annotation { "Feature Type Name" : "Feature", "Feature Type Description" : "" }
export const myFeature = defineFeature(function(context is Context, id is Id, definition is map)
    precondition{}
    {
        {
            var Q0;
            Q0=qCreatedBy(makeId("Top.planeOp"),FACE);
            var sketch = newSketch(context, id + "F0", { "sketchPlane" : qUnion([Q0])});
            skLineSegment(sketch, "E0.bottom", {"start": v(0, 0) * mm, "end": v(22.86, 0) * mm});
            skLineSegment(sketch, "E0.top", {"start": v(2.54, 25.4) * mm, "end": v(20.32, 25.4) * mm});
            skLineSegment(sketch, "E0.left", {"start": v(0, 0) * mm, "end": v(0, 22.86) * mm});
            skLineSegment(sketch, "E0.right", {"start": v(22.86, 0) * mm, "end": v(22.86, 22.86) * mm});
            skPoint(sketch, "E1.visualSharp", {"position": v(0, 25.4) * mm});
            skArc(sketch, "E1.filletArc", {"start": v(2.54, 25.4) * mm, "mid": v(0.74, 24.66) * mm, "end": v(0, 22.86) * mm});
            skPoint(sketch, "E2.visualSharp", {"position": v(22.86, 25.4) * mm});
            skArc(sketch, "E2.filletArc", {"start": v(22.86, 22.86) * mm, "mid": v(22.12, 24.66) * mm, "end": v(20.32, 25.4) * mm});
            skCircle(sketch, "E3", {"center": v(11.43, 2.54) * mm, "radius": 0.5 * mm});
            skPoint(sketch, "E4", {"position": v(11.43, 0) * mm});
            skCircle(sketch, "E5.1.0.0", {"center": v(13.97, 2.54) * mm, "radius": 0.5 * mm});
            skCircle(sketch, "E5.2.0.0", {"center": v(16.51, 2.54) * mm, "radius": 0.5 * mm});
            skCircle(sketch, "E5.3.0.0", {"center": v(19.05, 2.54) * mm, "radius": 0.5 * mm});
            skCircle(sketch, "E5.4.0.0", {"center": v(21.6, 2.54) * mm, "radius": 0.5 * mm});
            skLineSegment(sketch, "E5.direction1", {"start": v(11.43, 2.54) * mm, "end": v(13.97, 2.54) * mm, "construction": true});
            skCircle(sketch, "E6.1.0.0", {"center": v(8.9, 2.54) * mm, "radius": 0.5 * mm});
            skCircle(sketch, "E6.2.0.0", {"center": v(6.35, 2.54) * mm, "radius": 0.5 * mm});
            skCircle(sketch, "E6.3.0.0", {"center": v(3.8, 2.54) * mm, "radius": 0.5 * mm});
            skCircle(sketch, "E6.4.0.0", {"center": v(1.27, 2.54) * mm, "radius": 0.5 * mm});
            skLineSegment(sketch, "E6.direction1", {"start": v(11.43, 2.54) * mm, "end": v(8.9, 2.54) * mm, "construction": true});
            skCircle(sketch, "E7", {"center": v(2.54, 22.86) * mm, "radius": 1.27 * mm});
            skCircle(sketch, "E8", {"center": v(20.32, 22.86) * mm, "radius": 1.27 * mm});
            skLineSegment(sketch, "E9.bottom", {"start": v(-8.9, 0) * mm, "end": v(-24.13, 0) * mm});
            skLineSegment(sketch, "E9.top", {"start": v(-8.9, 20.32) * mm, "end": v(-24.13, 20.32) * mm});
            skLineSegment(sketch, "E9.left", {"start": v(-6.35, 2.54) * mm, "end": v(-6.35, 17.78) * mm});
            skLineSegment(sketch, "E9.right", {"start": v(-26.67, 2.54) * mm, "end": v(-26.67, 17.78) * mm});
            skPoint(sketch, "E10.visualSharp", {"position": v(-26.67, 20.32) * mm});
            skArc(sketch, "E10.filletArc", {"start": v(-24.13, 20.32) * mm, "mid": v(-25.93, 19.58) * mm, "end": v(-26.67, 17.78) * mm});
            skPoint(sketch, "E11.visualSharp", {"position": v(-6.35, 20.32) * mm});
            skArc(sketch, "E11.filletArc", {"start": v(-6.35, 17.78) * mm, "mid": v(-7.1, 19.58) * mm, "end": v(-8.9, 20.32) * mm});
            skPoint(sketch, "E12.visualSharp", {"position": v(-6.35, 0) * mm});
            skArc(sketch, "E12.filletArc", {"start": v(-8.9, 0) * mm, "mid": v(-7.1, 0.74) * mm, "end": v(-6.35, 2.54) * mm});
            skPoint(sketch, "E13.visualSharp", {"position": v(-26.67, 0) * mm});
            skArc(sketch, "E13.filletArc", {"start": v(-26.67, 2.54) * mm, "mid": v(-25.93, 0.74) * mm, "end": v(-24.13, 0) * mm});
            skCircle(sketch, "E14", {"center": v(-24.13, 17.78) * mm, "radius": 1.27 * mm});
            skCircle(sketch, "E15", {"center": v(-8.89, 17.78) * mm, "radius": 1.27 * mm});
            skCircle(sketch, "E16", {"center": v(-25.4, 2.54) * mm, "radius": 0.5 * mm});
            skCircle(sketch, "E17.1.0.0", {"center": v(-22.86, 2.54) * mm, "radius": 0.5 * mm});
            skCircle(sketch, "E17.2.0.0", {"center": v(-20.32, 2.54) * mm, "radius": 0.5 * mm});
            skCircle(sketch, "E17.3.0.0", {"center": v(-17.78, 2.54) * mm, "radius": 0.5 * mm});
            skCircle(sketch, "E17.4.0.0", {"center": v(-15.24, 2.54) * mm, "radius": 0.5 * mm});
            skCircle(sketch, "E17.5.0.0", {"center": v(-12.7, 2.54) * mm, "radius": 0.5 * mm});
            skCircle(sketch, "E17.6.0.0", {"center": v(-10.16, 2.54) * mm, "radius": 0.5 * mm});
            skCircle(sketch, "E17.7.0.0", {"center": v(-7.62, 2.54) * mm, "radius": 0.5 * mm});
            skLineSegment(sketch, "E17.direction1", {"start": v(-25.4, 2.54) * mm, "end": v(-22.86, 2.54) * mm, "construction": true});
            skLineSegment(sketch, "E18.bottom", {"start": v(-8.89, -6.35) * mm, "end": v(-24.13, -6.35) * mm});
            skLineSegment(sketch, "E18.top", {"start": v(-8.89, -26.67) * mm, "end": v(-24.13, -26.67) * mm});
            skLineSegment(sketch, "E18.left", {"start": v(-6.35, -8.89) * mm, "end": v(-6.35, -24.13) * mm});
            skLineSegment(sketch, "E18.right", {"start": v(-26.67, -8.9) * mm, "end": v(-26.67, -24.13) * mm});
            skPoint(sketch, "E19.visualSharp", {"position": v(-26.67, -6.35) * mm});
            skArc(sketch, "E19.filletArc", {"start": v(-24.13, -6.35) * mm, "mid": v(-25.93, -7.1) * mm, "end": v(-26.67, -8.9) * mm});
            skPoint(sketch, "E20.visualSharp", {"position": v(-6.35, -6.35) * mm});
            skArc(sketch, "E20.filletArc", {"start": v(-6.35, -8.89) * mm, "mid": v(-7.1, -7.1) * mm, "end": v(-8.89, -6.35) * mm});
            skPoint(sketch, "E21.visualSharp", {"position": v(-6.35, -26.67) * mm});
            skArc(sketch, "E21.filletArc", {"start": v(-8.89, -26.67) * mm, "mid": v(-7.1, -25.93) * mm, "end": v(-6.35, -24.13) * mm});
            skPoint(sketch, "E22.visualSharp", {"position": v(-26.67, -26.67) * mm});
            skArc(sketch, "E22.filletArc", {"start": v(-26.67, -24.13) * mm, "mid": v(-25.93, -25.93) * mm, "end": v(-24.13, -26.67) * mm});
            skCircle(sketch, "E23", {"center": v(-24.13, -8.9) * mm, "radius": 1.27 * mm});
            skCircle(sketch, "E24", {"center": v(-8.89, -8.89) * mm, "radius": 1.27 * mm});
            skCircle(sketch, "E25", {"center": v(-16.5, -25.15) * mm, "radius": 0.5 * mm});
            skPoint(sketch, "E25.centerSnap0", {"position": v(-16.5, -26.67) * mm});
            skCircle(sketch, "E26.1.0.0", {"center": v(-13.97, -25.15) * mm, "radius": 0.5 * mm});
            skCircle(sketch, "E26.2.0.0", {"center": v(-11.43, -25.15) * mm, "radius": 0.5 * mm});
            skCircle(sketch, "E26.3.0.0", {"center": v(-8.89, -25.15) * mm, "radius": 0.5 * mm});
            skLineSegment(sketch, "E26.direction1", {"start": v(-16.51, -25.15) * mm, "end": v(-13.97, -25.15) * mm, "construction": true});
            skCircle(sketch, "E27.1.0.0", {"center": v(-19.05, -25.15) * mm, "radius": 0.5 * mm});
            skCircle(sketch, "E27.2.0.0", {"center": v(-21.59, -25.15) * mm, "radius": 0.5 * mm});
            skCircle(sketch, "E27.3.0.0", {"center": v(-24.13, -25.15) * mm, "radius": 0.5 * mm});
            skLineSegment(sketch, "E27.direction1", {"start": v(-16.51, -25.15) * mm, "end": v(-19.05, -25.15) * mm, "construction": true});
            skCircle(sketch, "E28", {"center": v(-15.24, 15.24) * mm, "radius": 0.5 * mm});
            skCircle(sketch, "E29", {"center": v(-17.78, 15.24) * mm, "radius": 0.5 * mm});
            skCircle(sketch, "E30", {"center": v(-12.7, 15.24) * mm, "radius": 0.5 * mm});
            skLineSegment(sketch, "E31.bottom", {"start": v(2.54, -6.35) * mm, "end": v(21.59, -6.35) * mm});
            skLineSegment(sketch, "E31.top", {"start": v(2.54, -34.3) * mm, "end": v(21.59, -34.3) * mm});
            skLineSegment(sketch, "E31.left", {"start": v(0, -8.9) * mm, "end": v(0, -31.75) * mm});
            skLineSegment(sketch, "E31.right", {"start": v(24.13, -8.89) * mm, "end": v(24.13, -31.75) * mm});
            skPoint(sketch, "E32.visualSharp", {"position": v(0, -6.35) * mm});
            skArc(sketch, "E32.filletArc", {"start": v(2.54, -6.35) * mm, "mid": v(0.74, -7.1) * mm, "end": v(0, -8.9) * mm});
            skPoint(sketch, "E33.visualSharp", {"position": v(24.13, -6.35) * mm});
            skArc(sketch, "E33.filletArc", {"start": v(24.13, -8.89) * mm, "mid": v(23.39, -7.1) * mm, "end": v(21.59, -6.35) * mm});
            skPoint(sketch, "E34.visualSharp", {"position": v(0, -34.3) * mm});
            skArc(sketch, "E34.filletArc", {"start": v(0, -31.75) * mm, "mid": v(0.74, -33.55) * mm, "end": v(2.54, -34.3) * mm});
            skPoint(sketch, "E35.visualSharp", {"position": v(24.13, -34.3) * mm});
            skArc(sketch, "E35.filletArc", {"start": v(21.59, -34.3) * mm, "mid": v(23.39, -33.55) * mm, "end": v(24.13, -31.75) * mm});
            skCircle(sketch, "E36", {"center": v(21.59, -8.89) * mm, "radius": 1.27 * mm});
            skCircle(sketch, "E37", {"center": v(21.59, -31.75) * mm, "radius": 1.27 * mm});
            skCircle(sketch, "E38", {"center": v(2.54, -20.32) * mm, "radius": 0.5 * mm});
            skPoint(sketch, "E38.centerSnap0", {"position": v(0, -20.32) * mm});
            skCircle(sketch, "E39.0.1.0", {"center": v(2.54, -17.78) * mm, "radius": 0.5 * mm});
            skCircle(sketch, "E39.0.2.0", {"center": v(2.54, -15.24) * mm, "radius": 0.5 * mm});
            skCircle(sketch, "E39.0.3.0", {"center": v(2.54, -12.7) * mm, "radius": 0.5 * mm});
            skCircle(sketch, "E39.0.4.0", {"center": v(2.54, -10.16) * mm, "radius": 0.5 * mm});
            skLineSegment(sketch, "E39.direction1", {"start": v(0, -20.32) * mm, "end": v(2.54, -20.32) * mm, "construction": true});
            skLineSegment(sketch, "E39.direction2", {"start": v(2.54, -20.32) * mm, "end": v(2.54, -17.78) * mm, "construction": true});
            skCircle(sketch, "E40.0.1.0", {"center": v(2.54, -22.86) * mm, "radius": 0.5 * mm});
            skCircle(sketch, "E40.0.2.0", {"center": v(2.54, -25.4) * mm, "radius": 0.5 * mm});
            skCircle(sketch, "E40.0.3.0", {"center": v(2.54, -27.94) * mm, "radius": 0.5 * mm});
            skCircle(sketch, "E40.0.4.0", {"center": v(2.54, -30.48) * mm, "radius": 0.5 * mm});
            skLineSegment(sketch, "E40.direction2", {"start": v(2.54, -20.32) * mm, "end": v(2.54, -22.86) * mm, "construction": true});
            skCircle(sketch, "E41", {"center": v(14.48, -33.02) * mm, "radius": 0.5 * mm});
            skCircle(sketch, "E42.0.1.0", {"center": v(14.48, -30.48) * mm, "radius": 0.5 * mm});
            skCircle(sketch, "E42.1.0.0", {"center": v(11.94, -33.02) * mm, "radius": 0.5 * mm});
            skCircle(sketch, "E42.1.1.0", {"center": v(11.94, -30.48) * mm, "radius": 0.5 * mm});
            skCircle(sketch, "E42.2.0.0", {"center": v(9.4, -33.02) * mm, "radius": 0.5 * mm});
            skCircle(sketch, "E42.2.1.0", {"center": v(9.4, -30.48) * mm, "radius": 0.5 * mm});
            skCircle(sketch, "E42.3.0.0", {"center": v(6.86, -33.02) * mm, "radius": 0.5 * mm});
            skCircle(sketch, "E42.3.1.0", {"center": v(6.86, -30.48) * mm, "radius": 0.5 * mm});
            skLineSegment(sketch, "E42.direction1", {"start": v(14.48, -33.02) * mm, "end": v(11.94, -33.02) * mm, "construction": true});
            skLineSegment(sketch, "E42.direction2", {"start": v(14.48, -33.02) * mm, "end": v(14.48, -30.48) * mm, "construction": true});
            skLineSegment(sketch, "E43", {"start": v(11.94, -33.02) * mm, "end": v(9.4, -33.02) * mm, "construction": true});
            skPoint(sketch, "E44", {"position": v(10.67, -33.02) * mm});
            skCircle(sketch, "E45", {"center": v(20.07, -26.03) * mm, "radius": 0.5 * mm});
            skCircle(sketch, "E46", {"center": v(20.07, -22.48) * mm, "radius": 0.5 * mm});
            skCircle(sketch, "E47", {"center": v(20.07, -18.16) * mm, "radius": 0.5 * mm});
            skCircle(sketch, "E48", {"center": v(20.07, -14.6) * mm, "radius": 0.5 * mm});
            skLineSegment(sketch, "E49", {"start": v(20.07, -26.03) * mm, "end": v(20.07, -14.6) * mm, "construction": true});
            skPoint(sketch, "E50", {"position": v(20.07, -20.32) * mm});
            skLineSegment(sketch, "E51.bottom", {"start": v(31.75, 0) * mm, "end": v(47, 0) * mm});
            skLineSegment(sketch, "E51.top", {"start": v(31.75, 10.16) * mm, "end": v(47, 10.16) * mm});
            skLineSegment(sketch, "E51.left", {"start": v(29.21, 2.54) * mm, "end": v(29.21, 7.62) * mm});
            skLineSegment(sketch, "E51.right", {"start": v(49.53, 2.54) * mm, "end": v(49.53, 7.62) * mm});
            skPoint(sketch, "E52.visualSharp", {"position": v(29.21, 10.16) * mm});
            skArc(sketch, "E52.filletArc", {"start": v(31.75, 10.16) * mm, "mid": v(29.95, 9.42) * mm, "end": v(29.21, 7.62) * mm});
            skPoint(sketch, "E53.visualSharp", {"position": v(29.21, 0) * mm});
            skArc(sketch, "E53.filletArc", {"start": v(29.21, 2.54) * mm, "mid": v(29.95, 0.74) * mm, "end": v(31.75, 0) * mm});
            skPoint(sketch, "E54.visualSharp", {"position": v(49.53, 0) * mm});
            skArc(sketch, "E54.filletArc", {"start": v(47, 0) * mm, "mid": v(48.79, 0.74) * mm, "end": v(49.53, 2.54) * mm});
            skPoint(sketch, "E55.visualSharp", {"position": v(49.53, 10.16) * mm});
            skArc(sketch, "E55.filletArc", {"start": v(49.53, 7.62) * mm, "mid": v(48.79, 9.42) * mm, "end": v(47, 10.16) * mm});
            skCircle(sketch, "E56", {"center": v(31.75, 7.62) * mm, "radius": 1.27 * mm});
            skCircle(sketch, "E57", {"center": v(47, 7.62) * mm, "radius": 1.27 * mm});
            skCircle(sketch, "E58", {"center": v(39.37, 1.02) * mm, "radius": 0.5 * mm});
            skPoint(sketch, "E58.centerSnap0", {"position": v(39.37, 0) * mm});
            skCircle(sketch, "E59", {"center": v(36.83, 1.02) * mm, "radius": 0.5 * mm});
            skCircle(sketch, "E60", {"center": v(34.3, 1.02) * mm, "radius": 0.5 * mm});
            skCircle(sketch, "E61", {"center": v(41.91, 1.02) * mm, "radius": 0.5 * mm});
            skCircle(sketch, "E62", {"center": v(44.45, 1.02) * mm, "radius": 0.5 * mm});
            skLineSegment(sketch, "E63", {"start": v(34.3, 1.02) * mm, "end": v(36.83, 1.02) * mm, "construction": true});
            skLineSegment(sketch, "E64", {"start": v(36.83, 1.02) * mm, "end": v(39.37, 1.02) * mm, "construction": true});
            skLineSegment(sketch, "E65", {"start": v(39.37, 1.02) * mm, "end": v(41.91, 1.02) * mm, "construction": true});
            skLineSegment(sketch, "E66", {"start": v(41.91, 1.02) * mm, "end": v(44.45, 1.02) * mm, "construction": true});
            skLineSegment(sketch, "E67.bottom", {"start": v(31.75, -6.35) * mm, "end": v(45.72, -6.35) * mm});
            skLineSegment(sketch, "E67.top", {"start": v(31.75, -22.86) * mm, "end": v(45.72, -22.86) * mm});
            skLineSegment(sketch, "E67.left", {"start": v(29.21, -8.89) * mm, "end": v(29.21, -20.32) * mm});
            skLineSegment(sketch, "E67.right", {"start": v(48.26, -8.89) * mm, "end": v(48.26, -20.32) * mm});
            skPoint(sketch, "E68.visualSharp", {"position": v(29.21, -6.35) * mm});
            skArc(sketch, "E68.filletArc", {"start": v(31.75, -6.35) * mm, "mid": v(29.95, -7.1) * mm, "end": v(29.21, -8.89) * mm});
            skPoint(sketch, "E69.visualSharp", {"position": v(48.26, -6.35) * mm});
            skArc(sketch, "E69.filletArc", {"start": v(48.26, -8.89) * mm, "mid": v(47.52, -7.1) * mm, "end": v(45.72, -6.35) * mm});
            skPoint(sketch, "E70.visualSharp", {"position": v(48.26, -22.86) * mm});
            skArc(sketch, "E70.filletArc", {"start": v(45.72, -22.86) * mm, "mid": v(47.52, -22.12) * mm, "end": v(48.26, -20.32) * mm});
            skPoint(sketch, "E71.visualSharp", {"position": v(29.21, -22.86) * mm});
            skArc(sketch, "E71.filletArc", {"start": v(29.21, -20.32) * mm, "mid": v(29.95, -22.12) * mm, "end": v(31.75, -22.86) * mm});
            skCircle(sketch, "E72", {"center": v(45.72, -8.89) * mm, "radius": 1.27 * mm});
            skCircle(sketch, "E73", {"center": v(31.75, -8.89) * mm, "radius": 1.27 * mm});
            skCircle(sketch, "E74", {"center": v(38.74, -20.32) * mm, "radius": 0.5 * mm});
            skPoint(sketch, "E74.centerSnap0", {"position": v(38.74, -6.35) * mm});
            skCircle(sketch, "E75.1.0.0", {"center": v(41.28, -20.32) * mm, "radius": 0.5 * mm});
            skCircle(sketch, "E75.2.0.0", {"center": v(43.82, -20.32) * mm, "radius": 0.5 * mm});
            skCircle(sketch, "E75.3.0.0", {"center": v(46.36, -20.32) * mm, "radius": 0.5 * mm});
            skLineSegment(sketch, "E75.direction1", {"start": v(38.74, -20.32) * mm, "end": v(41.28, -20.32) * mm, "construction": true});
            skCircle(sketch, "E76.1.0.0", {"center": v(36.2, -20.32) * mm, "radius": 0.5 * mm});
            skCircle(sketch, "E76.2.0.0", {"center": v(33.66, -20.32) * mm, "radius": 0.5 * mm});
            skCircle(sketch, "E76.3.0.0", {"center": v(31.12, -20.32) * mm, "radius": 0.5 * mm});
            skLineSegment(sketch, "E76.direction1", {"start": v(38.74, -20.32) * mm, "end": v(36.2, -20.32) * mm, "construction": true});
            skLineSegment(sketch, "E77.bottom", {"start": v(31.75, 16.51) * mm, "end": v(47, 16.51) * mm});
            skLineSegment(sketch, "E77.top", {"start": v(31.75, 29.21) * mm, "end": v(47, 29.21) * mm});
            skLineSegment(sketch, "E77.left", {"start": v(29.21, 19.05) * mm, "end": v(29.21, 26.67) * mm});
            skLineSegment(sketch, "E77.right", {"start": v(49.53, 19.05) * mm, "end": v(49.53, 26.67) * mm});
            skPoint(sketch, "E78.visualSharp", {"position": v(29.21, 16.51) * mm});
            skArc(sketch, "E78.filletArc", {"start": v(29.21, 19.05) * mm, "mid": v(29.95, 17.25) * mm, "end": v(31.75, 16.51) * mm});
            skPoint(sketch, "E79.visualSharp", {"position": v(49.53, 29.2) * mm});
            skArc(sketch, "E79.filletArc", {"start": v(49.53, 26.67) * mm, "mid": v(48.79, 28.47) * mm, "end": v(47, 29.21) * mm});
            skPoint(sketch, "E80.visualSharp", {"position": v(29.21, 29.21) * mm});
            skArc(sketch, "E80.filletArc", {"start": v(31.75, 29.21) * mm, "mid": v(29.95, 28.47) * mm, "end": v(29.21, 26.67) * mm});
            skPoint(sketch, "E81.visualSharp", {"position": v(49.53, 16.51) * mm});
            skArc(sketch, "E81.filletArc", {"start": v(47, 16.51) * mm, "mid": v(48.79, 17.25) * mm, "end": v(49.53, 19.05) * mm});
            skCircle(sketch, "E82", {"center": v(47, 26.67) * mm, "radius": 1.27 * mm});
            skCircle(sketch, "E83", {"center": v(31.75, 26.67) * mm, "radius": 1.27 * mm});
            skCircle(sketch, "E84", {"center": v(40.64, 18.67) * mm, "radius": 0.5 * mm});
            skLineSegment(sketch, "E85", {"start": v(40.64, 18.67) * mm, "end": v(38.1, 18.67) * mm, "construction": true});
            skCircle(sketch, "E86", {"center": v(38.1, 18.67) * mm, "radius": 0.5 * mm});
            skPoint(sketch, "E87", {"position": v(39.37, 16.5) * mm});
            skPoint(sketch, "E88", {"position": v(39.37, 18.67) * mm});
            skCircle(sketch, "E89.1.0.0", {"center": v(43.18, 18.67) * mm, "radius": 0.5 * mm});
            skCircle(sketch, "E89.2.0.0", {"center": v(45.72, 18.67) * mm, "radius": 0.5 * mm});
            skLineSegment(sketch, "E89.direction1", {"start": v(40.64, 18.67) * mm, "end": v(43.18, 18.67) * mm, "construction": true});
            skCircle(sketch, "E90.0.3.0", {"center": v(48.26, 18.67) * mm, "radius": 0.5 * mm});
            skCircle(sketch, "E91.1.0.0", {"center": v(35.56, 18.67) * mm, "radius": 0.5 * mm});
            skCircle(sketch, "E91.2.0.0", {"center": v(33.02, 18.67) * mm, "radius": 0.5 * mm});
            skCircle(sketch, "E91.3.0.0", {"center": v(30.48, 18.67) * mm, "radius": 0.5 * mm});
            skLineSegment(sketch, "E91.direction1", {"start": v(38.1, 18.67) * mm, "end": v(35.56, 18.67) * mm, "construction": true});
            skSolve(sketch);
        }
        {
            var Q0;
            Q0=makeQuery(id+"F0.imprint","IMPRINT",FACE,{"disambiguationData":[TD([[makeQuery(id+"F0.imprint","IMPRINT",EDGE,{"derivedFrom":sQuery(id+"F0.wireOp",EDGE,"E0.bottom")}),1.0]])]});
            var Q1;
            Q1=makeQuery(id+"F0.imprint","IMPRINT",FACE,{"disambiguationData":[TD([[makeQuery(id+"F0.imprint","IMPRINT",EDGE,{"derivedFrom":sQuery(id+"F0.wireOp",EDGE,"E9.bottom")}),-1.0]])]});
            var Q2;
            Q2=makeQuery(id+"F0.imprint","IMPRINT",FACE,{"disambiguationData":[TD([[makeQuery(id+"F0.imprint","IMPRINT",EDGE,{"derivedFrom":sQuery(id+"F0.wireOp",EDGE,"E18.bottom")}),1.0]])]});
            var Q3;
            Q3=makeQuery(id+"F0.imprint","IMPRINT",FACE,{"disambiguationData":[TD([[makeQuery(id+"F0.imprint","IMPRINT",EDGE,{"derivedFrom":sQuery(id+"F0.wireOp",EDGE,"E31.bottom")}),-1.0]])]});
            var Q4;
            Q4=makeQuery(id+"F0.imprint","IMPRINT",FACE,{"disambiguationData":[TD([[makeQuery(id+"F0.imprint","IMPRINT",EDGE,{"derivedFrom":sQuery(id+"F0.wireOp",EDGE,"E67.bottom")}),-1.0]])]});
            var Q5;
            Q5=makeQuery(id+"F0.imprint","IMPRINT",FACE,{"disambiguationData":[TD([[makeQuery(id+"F0.imprint","IMPRINT",EDGE,{"derivedFrom":sQuery(id+"F0.wireOp",EDGE,"E77.bottom")}),1.0]])]});
            extrude(context, id + "F1", {"entities" : qUnion([Q0, Q1, Q2, Q3, Q4, Q5]), "depth" : 1.59 * mm});
        }
        {
            var Q0;
            Q0=makeQuery(id+"F0.imprint","IMPRINT",FACE,{"disambiguationData":[TD([[makeQuery(id+"F0.imprint","IMPRINT",EDGE,{"derivedFrom":sQuery(id+"F0.wireOp",EDGE,"E51.bottom")}),1.0]])]});
            extrude(context, id + "F2", {"entities" : qUnion([Q0]), "depth" : 0.8 * mm});
        }
        {
            var Q0;
            Q0=makeQuery(id+"F1.opExtrude","CAP_FACE",FACE,{"disambiguationData":[OSD([sQuery(id+"F0.wireOp",EDGE,"E0.bottom"),sQuery(id+"F0.wireOp",EDGE,"E0.top"),sQuery(id+"F0.wireOp",EDGE,"E0.left"),sQuery(id+"F0.wireOp",EDGE,"E0.right"),sQuery(id+"F0.wireOp",EDGE,"E1.filletArc"),sQuery(id+"F0.wireOp",EDGE,"E2.filletArc"),sQuery(id+"F0.wireOp",EDGE,"E3"),sQuery(id+"F0.wireOp",EDGE,"E5.1.0.0"),sQuery(id+"F0.wireOp",EDGE,"E5.2.0.0"),sQuery(id+"F0.wireOp",EDGE,"E5.3.0.0"),sQuery(id+"F0.wireOp",EDGE,"E5.4.0.0"),sQuery(id+"F0.wireOp",EDGE,"E6.1.0.0"),sQuery(id+"F0.wireOp",EDGE,"E6.2.0.0"),sQuery(id+"F0.wireOp",EDGE,"E6.3.0.0"),sQuery(id+"F0.wireOp",EDGE,"E6.4.0.0"),sQuery(id+"F0.wireOp",EDGE,"E7"),sQuery(id+"F0.wireOp",EDGE,"E8")])],"isStart":false});
            var sketch = newSketch(context, id + "F3", { "sketchPlane" : qUnion([Q0])});
            skLineSegment(sketch, "E92.bottom", {"start": v(6.35, 24.9) * mm, "end": v(16.5, 24.9) * mm});
            skLineSegment(sketch, "E92.top", {"start": v(6.35, 7.11) * mm, "end": v(16.5, 7.11) * mm});
            skLineSegment(sketch, "E92.left", {"start": v(6.35, 24.9) * mm, "end": v(6.35, 7.11) * mm});
            skLineSegment(sketch, "E92.right", {"start": v(16.51, 24.9) * mm, "end": v(16.51, 7.11) * mm});
            skPoint(sketch, "E93", {"position": v(11.43, 25.4) * mm});
            skPoint(sketch, "E94", {"position": v(11.43, 24.9) * mm});
            skLineSegment(sketch, "E95.bottom", {"start": v(2.18, 19.3) * mm, "end": v(4.47, 19.3) * mm});
            skLineSegment(sketch, "E95.top", {"start": v(2.18, 18.03) * mm, "end": v(4.47, 18.03) * mm});
            skLineSegment(sketch, "E95.left", {"start": v(2.18, 19.3) * mm, "end": v(2.18, 18.03) * mm});
            skLineSegment(sketch, "E95.right", {"start": v(4.47, 19.3) * mm, "end": v(4.47, 18.03) * mm});
            skLineSegment(sketch, "E96.bottom", {"start": v(2.18, 16.9) * mm, "end": v(4.47, 16.9) * mm});
            skLineSegment(sketch, "E96.top", {"start": v(2.18, 15.62) * mm, "end": v(4.47, 15.62) * mm});
            skLineSegment(sketch, "E96.left", {"start": v(2.18, 16.9) * mm, "end": v(2.18, 15.62) * mm});
            skLineSegment(sketch, "E96.right", {"start": v(4.47, 16.9) * mm, "end": v(4.47, 15.62) * mm});
            skLineSegment(sketch, "E97.bottom", {"start": v(2.18, 15.24) * mm, "end": v(4.47, 15.24) * mm});
            skLineSegment(sketch, "E97.top", {"start": v(2.18, 13.97) * mm, "end": v(4.47, 13.97) * mm});
            skLineSegment(sketch, "E97.left", {"start": v(2.18, 15.24) * mm, "end": v(2.18, 13.97) * mm});
            skLineSegment(sketch, "E97.right", {"start": v(4.47, 15.24) * mm, "end": v(4.47, 13.97) * mm});
            skLineSegment(sketch, "E98.bottom", {"start": v(2.18, 13.33) * mm, "end": v(4.47, 13.33) * mm});
            skLineSegment(sketch, "E98.top", {"start": v(2.18, 12.06) * mm, "end": v(4.47, 12.06) * mm});
            skLineSegment(sketch, "E98.left", {"start": v(2.18, 13.33) * mm, "end": v(2.18, 12.06) * mm});
            skLineSegment(sketch, "E98.right", {"start": v(4.47, 13.33) * mm, "end": v(4.47, 12.06) * mm});
            skLineSegment(sketch, "E99.bottom", {"start": v(2.44, 10.77) * mm, "end": v(4.22, 10.77) * mm});
            skLineSegment(sketch, "E99.top", {"start": v(2.44, 7.82) * mm, "end": v(4.22, 7.82) * mm});
            skLineSegment(sketch, "E99.left", {"start": v(2.44, 10.77) * mm, "end": v(2.44, 7.82) * mm});
            skLineSegment(sketch, "E99.right", {"start": v(4.22, 10.77) * mm, "end": v(4.22, 7.82) * mm});
            skLineSegment(sketch, "E100.bottom", {"start": v(18.22, 5.2) * mm, "end": v(19.5, 5.2) * mm});
            skLineSegment(sketch, "E100.top", {"start": v(18.22, 7.24) * mm, "end": v(19.5, 7.24) * mm});
            skLineSegment(sketch, "E100.left", {"start": v(18.22, 7.24) * mm, "end": v(18.22, 5.2) * mm});
            skLineSegment(sketch, "E100.right", {"start": v(19.5, 7.24) * mm, "end": v(19.5, 5.2) * mm});
            skLineSegment(sketch, "E101.bottom", {"start": v(20.26, 7.24) * mm, "end": v(21.53, 7.24) * mm});
            skLineSegment(sketch, "E101.top", {"start": v(20.26, 5.2) * mm, "end": v(21.53, 5.2) * mm});
            skLineSegment(sketch, "E101.left", {"start": v(20.26, 7.24) * mm, "end": v(20.26, 5.2) * mm});
            skLineSegment(sketch, "E101.right", {"start": v(21.53, 7.24) * mm, "end": v(21.53, 5.2) * mm});
            skLineSegment(sketch, "E102.bottom", {"start": v(18.99, 11.68) * mm, "end": v(20.76, 11.68) * mm});
            skLineSegment(sketch, "E102.top", {"start": v(18.99, 8.76) * mm, "end": v(20.76, 8.76) * mm});
            skLineSegment(sketch, "E102.left", {"start": v(18.99, 11.68) * mm, "end": v(18.99, 8.76) * mm});
            skLineSegment(sketch, "E102.right", {"start": v(20.76, 11.68) * mm, "end": v(20.76, 8.76) * mm});
            skLineSegment(sketch, "E103.bottom", {"start": v(18.41, 13.33) * mm, "end": v(21.34, 13.33) * mm});
            skLineSegment(sketch, "E103.top", {"start": v(18.41, 14.6) * mm, "end": v(21.34, 14.6) * mm});
            skLineSegment(sketch, "E103.left", {"start": v(18.41, 13.33) * mm, "end": v(18.41, 14.6) * mm});
            skLineSegment(sketch, "E103.right", {"start": v(21.34, 13.33) * mm, "end": v(21.34, 14.6) * mm});
            skLineSegment(sketch, "E104.bottom", {"start": v(18.8, 16.13) * mm, "end": v(20.96, 16.13) * mm});
            skLineSegment(sketch, "E104.top", {"start": v(18.8, 17.4) * mm, "end": v(20.96, 17.4) * mm});
            skLineSegment(sketch, "E104.left", {"start": v(18.8, 16.13) * mm, "end": v(18.8, 17.4) * mm});
            skLineSegment(sketch, "E104.right", {"start": v(20.95, 16.13) * mm, "end": v(20.95, 17.4) * mm});
            skLineSegment(sketch, "E105.bottom", {"start": v(18.8, 18.03) * mm, "end": v(20.95, 18.03) * mm});
            skLineSegment(sketch, "E105.top", {"start": v(18.8, 19.3) * mm, "end": v(20.95, 19.3) * mm});
            skLineSegment(sketch, "E105.left", {"start": v(18.8, 18.03) * mm, "end": v(18.8, 19.3) * mm});
            skLineSegment(sketch, "E105.right", {"start": v(20.95, 18.03) * mm, "end": v(20.95, 19.3) * mm});
            skLineSegment(sketch, "E106.bottom", {"start": v(2.18, 6.86) * mm, "end": v(4.47, 6.86) * mm});
            skLineSegment(sketch, "E106.top", {"start": v(2.18, 5.59) * mm, "end": v(4.47, 5.59) * mm});
            skLineSegment(sketch, "E106.left", {"start": v(2.18, 6.86) * mm, "end": v(2.18, 5.59) * mm});
            skLineSegment(sketch, "E106.right", {"start": v(4.47, 6.86) * mm, "end": v(4.47, 5.59) * mm});
            skPoint(sketch, "E107", {"position": v(3.33, 12.06) * mm});
            skPoint(sketch, "E108", {"position": v(3.33, 10.77) * mm});
            skPoint(sketch, "E109", {"position": v(19.88, 18.03) * mm});
            skPoint(sketch, "E110", {"position": v(19.88, 14.6) * mm});
            skPoint(sketch, "E111", {"position": v(19.88, 11.68) * mm});
            skLineSegment(sketch, "E112", {"start": v(19.5, 6.22) * mm, "end": v(20.26, 6.22) * mm, "construction": true});
            skPoint(sketch, "E113", {"position": v(19.88, 6.22) * mm});
            skLineSegment(sketch, "E114.bottom", {"start": v(6.1, 23.62) * mm, "end": v(4.83, 23.62) * mm});
            skLineSegment(sketch, "E114.top", {"start": v(6.1, 22.35) * mm, "end": v(4.83, 22.35) * mm});
            skLineSegment(sketch, "E114.left", {"start": v(6.1, 23.62) * mm, "end": v(6.1, 22.35) * mm});
            skLineSegment(sketch, "E114.right", {"start": v(4.83, 23.62) * mm, "end": v(4.83, 22.35) * mm});
            skLineSegment(sketch, "E115.bottom", {"start": v(18.03, 23.62) * mm, "end": v(16.76, 23.62) * mm});
            skLineSegment(sketch, "E115.top", {"start": v(18.03, 22.35) * mm, "end": v(16.76, 22.35) * mm});
            skLineSegment(sketch, "E115.left", {"start": v(18.03, 23.62) * mm, "end": v(18.03, 22.35) * mm});
            skLineSegment(sketch, "E115.right", {"start": v(16.76, 23.62) * mm, "end": v(16.76, 22.35) * mm});
            skSolve(sketch);
        }
        {
            var Q0;
            Q0=makeQuery(id+"F3.imprint","IMPRINT",FACE,{"disambiguationData":[TD([[makeQuery(id+"F3.imprint","IMPRINT",EDGE,{"derivedFrom":sQuery(id+"F3.wireOp",EDGE,"E92.bottom")}),-1.0]])]});
            var Q1;
            Q1=makeQuery(id+"F3.imprint","IMPRINT",FACE,{"disambiguationData":[TD([[makeQuery(id+"F3.imprint","IMPRINT",EDGE,{"derivedFrom":sQuery(id+"F3.wireOp",EDGE,"E114.bottom")}),1.0]])]});
            var Q2;
            Q2=makeQuery(id+"F3.imprint","IMPRINT",FACE,{"disambiguationData":[TD([[makeQuery(id+"F3.imprint","IMPRINT",EDGE,{"derivedFrom":sQuery(id+"F3.wireOp",EDGE,"E115.bottom")}),1.0]])]});
            var Q3;
            Q3=makeQuery(id+"F3.imprint","IMPRINT",FACE,{"disambiguationData":[TD([[makeQuery(id+"F3.imprint","IMPRINT",EDGE,{"derivedFrom":sQuery(id+"F3.wireOp",EDGE,"E105.bottom")}),1.0]])]});
            var Q4;
            Q4=makeQuery(id+"F3.imprint","IMPRINT",FACE,{"disambiguationData":[TD([[makeQuery(id+"F3.imprint","IMPRINT",EDGE,{"derivedFrom":sQuery(id+"F3.wireOp",EDGE,"E104.bottom")}),1.0]])]});
            var Q5;
            Q5=makeQuery(id+"F3.imprint","IMPRINT",FACE,{"disambiguationData":[TD([[makeQuery(id+"F3.imprint","IMPRINT",EDGE,{"derivedFrom":sQuery(id+"F3.wireOp",EDGE,"E103.bottom")}),1.0]])]});
            var Q6;
            Q6=makeQuery(id+"F3.imprint","IMPRINT",FACE,{"disambiguationData":[TD([[makeQuery(id+"F3.imprint","IMPRINT",EDGE,{"derivedFrom":sQuery(id+"F3.wireOp",EDGE,"E102.bottom")}),-1.0]])]});
            var Q7;
            Q7=makeQuery(id+"F3.imprint","IMPRINT",FACE,{"disambiguationData":[TD([[makeQuery(id+"F3.imprint","IMPRINT",EDGE,{"derivedFrom":sQuery(id+"F3.wireOp",EDGE,"E101.bottom")}),-1.0]])]});
            var Q8;
            Q8=makeQuery(id+"F3.imprint","IMPRINT",FACE,{"disambiguationData":[TD([[makeQuery(id+"F3.imprint","IMPRINT",EDGE,{"derivedFrom":sQuery(id+"F3.wireOp",EDGE,"E100.bottom")}),1.0]])]});
            var Q9;
            Q9=makeQuery(id+"F3.imprint","IMPRINT",FACE,{"disambiguationData":[TD([[makeQuery(id+"F3.imprint","IMPRINT",EDGE,{"derivedFrom":sQuery(id+"F3.wireOp",EDGE,"E106.bottom")}),-1.0]])]});
            var Q10;
            Q10=makeQuery(id+"F3.imprint","IMPRINT",FACE,{"disambiguationData":[TD([[makeQuery(id+"F3.imprint","IMPRINT",EDGE,{"derivedFrom":sQuery(id+"F3.wireOp",EDGE,"E99.bottom")}),-1.0]])]});
            var Q11;
            Q11=makeQuery(id+"F3.imprint","IMPRINT",FACE,{"disambiguationData":[TD([[makeQuery(id+"F3.imprint","IMPRINT",EDGE,{"derivedFrom":sQuery(id+"F3.wireOp",EDGE,"E98.bottom")}),-1.0]])]});
            var Q12;
            Q12=makeQuery(id+"F3.imprint","IMPRINT",FACE,{"disambiguationData":[TD([[makeQuery(id+"F3.imprint","IMPRINT",EDGE,{"derivedFrom":sQuery(id+"F3.wireOp",EDGE,"E95.bottom")}),-1.0]])]});
            var Q13;
            Q13=makeQuery(id+"F3.imprint","IMPRINT",FACE,{"disambiguationData":[TD([[makeQuery(id+"F3.imprint","IMPRINT",EDGE,{"derivedFrom":sQuery(id+"F3.wireOp",EDGE,"E96.bottom")}),-1.0]])]});
            var Q14;
            Q14=makeQuery(id+"F3.imprint","IMPRINT",FACE,{"disambiguationData":[TD([[makeQuery(id+"F3.imprint","IMPRINT",EDGE,{"derivedFrom":sQuery(id+"F3.wireOp",EDGE,"E97.bottom")}),-1.0]])]});
            extrude(context, id + "F4", {"entities" : qUnion([Q0, Q1, Q2, Q3, Q4, Q5, Q6, Q7, Q8, Q9, Q10, Q11, Q12, Q13, Q14]), "operationType" : NewBodyOperationType.ADD, "depth" : 0.8 * mm});
        }
        {
            var Q0;
            Q0=makeQuery(id+"F4.opExtrude","CAP_FACE",FACE,{"disambiguationData":[OSD([sQuery(id+"F3.wireOp",EDGE,"E92.bottom"),sQuery(id+"F3.wireOp",EDGE,"E92.top"),sQuery(id+"F3.wireOp",EDGE,"E92.left"),sQuery(id+"F3.wireOp",EDGE,"E92.right")])],"isStart":false});
            var sketch = newSketch(context, id + "F5", { "sketchPlane" : qUnion([Q0])});
            skLineSegment(sketch, "E116.bottom", {"start": v(6.86, 21.2) * mm, "end": v(16, 21.2) * mm});
            skLineSegment(sketch, "E116.top", {"start": v(6.86, 7.62) * mm, "end": v(16, 7.62) * mm});
            skLineSegment(sketch, "E116.left", {"start": v(6.86, 21.2) * mm, "end": v(6.86, 7.62) * mm});
            skLineSegment(sketch, "E116.right", {"start": v(16, 21.2) * mm, "end": v(16, 7.62) * mm});
            skLineSegment(sketch, "E117.bottom", {"start": v(6.86, 24.38) * mm, "end": v(13.87, 24.38) * mm});
            skLineSegment(sketch, "E117.top", {"start": v(6.86, 22.45) * mm, "end": v(13.87, 22.45) * mm});
            skLineSegment(sketch, "E117.left", {"start": v(6.86, 24.38) * mm, "end": v(6.86, 22.45) * mm});
            skLineSegment(sketch, "E117.right", {"start": v(13.87, 24.38) * mm, "end": v(13.87, 22.45) * mm});
            skSolve(sketch);
        }
        {
            var Q0;
            Q0=makeQuery(id+"F5.imprint","IMPRINT",FACE,{"disambiguationData":[TD([[makeQuery(id+"F5.imprint","IMPRINT",EDGE,{"derivedFrom":sQuery(id+"F5.wireOp",EDGE,"E116.bottom")}),-1.0]])]});
            var Q1;
            Q1=makeQuery(id+"F5.imprint","IMPRINT",FACE,{"disambiguationData":[TD([[makeQuery(id+"F5.imprint","IMPRINT",EDGE,{"derivedFrom":sQuery(id+"F5.wireOp",EDGE,"E117.bottom")}),-1.0]])]});
            extrude(context, id + "F6", {"entities" : qUnion([Q0, Q1]), "operationType" : NewBodyOperationType.ADD, "depth" : 1.59 * mm});
        }
        {
            var Q0;
            Q0=makeQuery(id+"F1.opExtrude","CAP_FACE",FACE,{"disambiguationData":[OSD([sQuery(id+"F0.wireOp",EDGE,"E0.bottom"),sQuery(id+"F0.wireOp",EDGE,"E0.top"),sQuery(id+"F0.wireOp",EDGE,"E0.left"),sQuery(id+"F0.wireOp",EDGE,"E0.right"),sQuery(id+"F0.wireOp",EDGE,"E1.filletArc"),sQuery(id+"F0.wireOp",EDGE,"E2.filletArc"),sQuery(id+"F0.wireOp",EDGE,"E3"),sQuery(id+"F0.wireOp",EDGE,"E5.1.0.0"),sQuery(id+"F0.wireOp",EDGE,"E5.2.0.0"),sQuery(id+"F0.wireOp",EDGE,"E5.3.0.0"),sQuery(id+"F0.wireOp",EDGE,"E5.4.0.0"),sQuery(id+"F0.wireOp",EDGE,"E6.1.0.0"),sQuery(id+"F0.wireOp",EDGE,"E6.2.0.0"),sQuery(id+"F0.wireOp",EDGE,"E6.3.0.0"),sQuery(id+"F0.wireOp",EDGE,"E6.4.0.0"),sQuery(id+"F0.wireOp",EDGE,"E7"),sQuery(id+"F0.wireOp",EDGE,"E8")])],"isStart":true});
            var sketch = newSketch(context, id + "F7", { "sketchPlane" : qUnion([Q0])});
            skLineSegment(sketch, "E118.bottom", {"start": v(0, -1.27) * mm, "end": v(22.86, -1.27) * mm});
            skLineSegment(sketch, "E118.top", {"start": v(0, -3.81) * mm, "end": v(22.86, -3.81) * mm});
            skLineSegment(sketch, "E118.left", {"start": v(0, -1.27) * mm, "end": v(0, -3.81) * mm});
            skLineSegment(sketch, "E118.right", {"start": v(22.86, -1.27) * mm, "end": v(22.86, -3.8) * mm});
            skPoint(sketch, "E119", {"position": v(0, -2.54) * mm});
            skPoint(sketch, "E120", {"position": v(11.43, -1.27) * mm});
            skPoint(sketch, "E121", {"position": v(11.43, -2.54) * mm});
            skLineSegment(sketch, "E122.bottom", {"start": v(33.02, 0.25) * mm, "end": v(45.72, 0.25) * mm});
            skLineSegment(sketch, "E122.top", {"start": v(33.02, -2.29) * mm, "end": v(45.72, -2.29) * mm});
            skLineSegment(sketch, "E122.left", {"start": v(33.02, 0.25) * mm, "end": v(33.02, -2.29) * mm});
            skLineSegment(sketch, "E122.right", {"start": v(45.72, 0.25) * mm, "end": v(45.72, -2.29) * mm});
            skPoint(sketch, "E123", {"position": v(39.37, 0.25) * mm});
            skPoint(sketch, "E124", {"position": v(33.02, -1.02) * mm});
            skCircle(sketch, "E125.0", {"center": v(39.37, -1.02) * mm, "radius": 0.5 * mm, "construction": true});
            skLineSegment(sketch, "E126.bottom", {"start": v(-19.05, -13.97) * mm, "end": v(-11.43, -13.97) * mm});
            skLineSegment(sketch, "E126.top", {"start": v(-19.05, -16.51) * mm, "end": v(-11.43, -16.51) * mm});
            skLineSegment(sketch, "E126.left", {"start": v(-19.05, -13.97) * mm, "end": v(-19.05, -16.51) * mm});
            skLineSegment(sketch, "E126.right", {"start": v(-11.43, -13.97) * mm, "end": v(-11.43, -16.51) * mm});
            skLineSegment(sketch, "E127.bottom", {"start": v(-26.67, -1.27) * mm, "end": v(-6.35, -1.27) * mm});
            skLineSegment(sketch, "E127.top", {"start": v(-26.67, -3.81) * mm, "end": v(-6.35, -3.81) * mm});
            skLineSegment(sketch, "E127.left", {"start": v(-26.67, -1.27) * mm, "end": v(-26.67, -3.8) * mm});
            skLineSegment(sketch, "E127.right", {"start": v(-6.35, -1.27) * mm, "end": v(-6.35, -3.8) * mm});
            skCircle(sketch, "E128.0", {"center": v(-15.24, -15.24) * mm, "radius": 0.5 * mm});
            skPoint(sketch, "E129", {"position": v(-16.51, -1.27) * mm});
            skPoint(sketch, "E130", {"position": v(-26.67, -2.54) * mm});
            skPoint(sketch, "E131", {"position": v(-15.24, -13.97) * mm});
            skPoint(sketch, "E132", {"position": v(-19.05, -15.24) * mm});
            skCircle(sketch, "E133.0", {"center": v(-17.78, -2.54) * mm, "radius": 0.5 * mm, "construction": true});
            skCircle(sketch, "E134.0", {"center": v(-15.24, -2.54) * mm, "radius": 0.5 * mm, "construction": true});
            skLineSegment(sketch, "E135", {"start": v(-17.78, -2.54) * mm, "end": v(-15.24, -2.54) * mm, "construction": true});
            skPoint(sketch, "E136", {"position": v(-16.51, -2.54) * mm});
            skLineSegment(sketch, "E137.bottom", {"start": v(-25.4, 26.42) * mm, "end": v(-7.62, 26.42) * mm});
            skLineSegment(sketch, "E137.top", {"start": v(-25.4, 23.88) * mm, "end": v(-7.62, 23.88) * mm});
            skLineSegment(sketch, "E137.left", {"start": v(-25.4, 26.42) * mm, "end": v(-25.4, 23.88) * mm});
            skLineSegment(sketch, "E137.right", {"start": v(-7.62, 26.42) * mm, "end": v(-7.62, 23.88) * mm});
            skCircle(sketch, "E138.0", {"center": v(-16.5, 25.15) * mm, "radius": 0.5 * mm, "construction": true});
            skPoint(sketch, "E139", {"position": v(-16.5, 26.42) * mm});
            skPoint(sketch, "E140", {"position": v(-25.4, 25.15) * mm});
            skLineSegment(sketch, "E141.bottom", {"start": v(3.8, 31.75) * mm, "end": v(1.27, 31.75) * mm});
            skLineSegment(sketch, "E141.top", {"start": v(3.8, 8.9) * mm, "end": v(1.27, 8.9) * mm});
            skLineSegment(sketch, "E141.left", {"start": v(3.81, 31.75) * mm, "end": v(3.81, 8.9) * mm});
            skLineSegment(sketch, "E141.right", {"start": v(1.27, 31.75) * mm, "end": v(1.27, 8.9) * mm});
            skCircle(sketch, "E142.0", {"center": v(2.54, 20.32) * mm, "radius": 0.5 * mm, "construction": true});
            skPoint(sketch, "E143", {"position": v(2.54, 31.75) * mm});
            skPoint(sketch, "E144", {"position": v(1.27, 20.32) * mm});
            skLineSegment(sketch, "E145.bottom", {"start": v(47.63, 19.05) * mm, "end": v(29.85, 19.05) * mm});
            skLineSegment(sketch, "E145.top", {"start": v(47.63, 21.59) * mm, "end": v(29.85, 21.59) * mm});
            skLineSegment(sketch, "E145.left", {"start": v(47.63, 19.05) * mm, "end": v(47.63, 21.59) * mm});
            skLineSegment(sketch, "E145.right", {"start": v(29.85, 19.05) * mm, "end": v(29.85, 21.59) * mm});
            skPoint(sketch, "E146", {"position": v(38.74, 21.59) * mm});
            skPoint(sketch, "E147", {"position": v(47.63, 20.32) * mm});
            skCircle(sketch, "E148.0", {"center": v(38.74, 20.32) * mm, "radius": 0.5 * mm, "construction": true});
            skCircle(sketch, "E149.0", {"center": v(38.1, -18.67) * mm, "radius": 0.5 * mm, "construction": true});
            skCircle(sketch, "E150.0", {"center": v(40.64, -18.67) * mm, "radius": 0.5 * mm, "construction": true});
            skLineSegment(sketch, "E151", {"start": v(38.1, -18.67) * mm, "end": v(40.64, -18.67) * mm, "construction": true});
            skLineSegment(sketch, "E152.bottom", {"start": v(29.21, -17.4) * mm, "end": v(49.53, -17.4) * mm});
            skLineSegment(sketch, "E152.top", {"start": v(29.21, -19.94) * mm, "end": v(49.53, -19.94) * mm});
            skLineSegment(sketch, "E152.left", {"start": v(29.21, -17.4) * mm, "end": v(29.21, -19.94) * mm});
            skLineSegment(sketch, "E152.right", {"start": v(49.53, -17.4) * mm, "end": v(49.53, -19.94) * mm});
            skPoint(sketch, "E152.middle", {"position": v(39.37, -18.67) * mm});
            skSolve(sketch);
        }
        {
            var Q0;
            Q0=makeQuery(id+"F7.imprint","IMPRINT",FACE,{"disambiguationData":[TD([[makeQuery(id+"F7.imprint","IMPRINT",EDGE,{"derivedFrom":sQuery(id+"F7.wireOp",EDGE,"E137.bottom")}),-1.0]])]});
            var Q1;
            Q1=makeQuery(id+"F7.imprint","IMPRINT",FACE,{"disambiguationData":[TD([[makeQuery(id+"F7.imprint","IMPRINT",EDGE,{"derivedFrom":sQuery(id+"F7.wireOp",EDGE,"E127.bottom")}),-1.0]])]});
            var Q2;
            Q2=makeQuery(id+"F7.imprint","IMPRINT",FACE,{"disambiguationData":[TD([[makeQuery(id+"F7.imprint","IMPRINT",EDGE,{"derivedFrom":sQuery(id+"F7.wireOp",EDGE,"E126.bottom")}),-1.0]])]});
            var Q3;
            Q3=makeQuery(id+"F7.imprint","IMPRINT",FACE,{"disambiguationData":[TD([[makeQuery(id+"F7.imprint","IMPRINT",EDGE,{"derivedFrom":sQuery(id+"F7.wireOp",EDGE,"E141.bottom")}),1.0]])]});
            var Q4;
            Q4=makeQuery(id+"F7.imprint","IMPRINT",FACE,{"disambiguationData":[TD([[makeQuery(id+"F7.imprint","IMPRINT",EDGE,{"derivedFrom":sQuery(id+"F7.wireOp",EDGE,"E122.bottom")}),-1.0]])]});
            var Q5;
            Q5=makeQuery(id+"F7.imprint","IMPRINT",FACE,{"disambiguationData":[TD([[makeQuery(id+"F7.imprint","IMPRINT",EDGE,{"derivedFrom":makeQuery(id+"F1.opExtrude","CAP_EDGE",EDGE,{"disambiguationData":[OSD([sQuery(id+"F0.wireOp",EDGE,"E6.4.0.0")])],"isStart":true})}),-1.0]])]});
            var Q6;
            Q6=makeQuery(id+"F7.imprint","IMPRINT",FACE,{"disambiguationData":[TD([[makeQuery(id+"F7.imprint","IMPRINT",EDGE,{"derivedFrom":makeQuery(id+"F1.opExtrude","CAP_EDGE",EDGE,{"disambiguationData":[OSD([sQuery(id+"F0.wireOp",EDGE,"E6.2.0.0")])],"isStart":true})}),-1.0]])]});
            var Q7;
            Q7=makeQuery(id+"F7.imprint","IMPRINT",FACE,{"disambiguationData":[TD([[makeQuery(id+"F7.imprint","IMPRINT",EDGE,{"derivedFrom":makeQuery(id+"F1.opExtrude","CAP_EDGE",EDGE,{"disambiguationData":[OSD([sQuery(id+"F0.wireOp",EDGE,"E6.3.0.0")])],"isStart":true})}),-1.0]])]});
            var Q8;
            Q8=makeQuery(id+"F7.imprint","IMPRINT",FACE,{"disambiguationData":[TD([[makeQuery(id+"F7.imprint","IMPRINT",EDGE,{"derivedFrom":makeQuery(id+"F1.opExtrude","CAP_EDGE",EDGE,{"disambiguationData":[OSD([sQuery(id+"F0.wireOp",EDGE,"E6.1.0.0")])],"isStart":true})}),-1.0]])]});
            var Q9;
            Q9=makeQuery(id+"F7.imprint","IMPRINT",FACE,{"disambiguationData":[TD([[makeQuery(id+"F7.imprint","IMPRINT",EDGE,{"derivedFrom":makeQuery(id+"F1.opExtrude","CAP_EDGE",EDGE,{"disambiguationData":[OSD([sQuery(id+"F0.wireOp",EDGE,"E3")])],"isStart":true})}),-1.0]])]});
            var Q10;
            Q10=makeQuery(id+"F7.imprint","IMPRINT",FACE,{"disambiguationData":[TD([[makeQuery(id+"F7.imprint","IMPRINT",EDGE,{"derivedFrom":makeQuery(id+"F1.opExtrude","CAP_EDGE",EDGE,{"disambiguationData":[OSD([sQuery(id+"F0.wireOp",EDGE,"E5.2.0.0")])],"isStart":true})}),-1.0]])]});
            var Q11;
            Q11=makeQuery(id+"F7.imprint","IMPRINT",FACE,{"disambiguationData":[TD([[makeQuery(id+"F7.imprint","IMPRINT",EDGE,{"derivedFrom":makeQuery(id+"F1.opExtrude","CAP_EDGE",EDGE,{"disambiguationData":[OSD([sQuery(id+"F0.wireOp",EDGE,"E5.3.0.0")])],"isStart":true})}),-1.0]])]});
            var Q12;
            Q12=makeQuery(id+"F7.imprint","IMPRINT",FACE,{"disambiguationData":[TD([[makeQuery(id+"F7.imprint","IMPRINT",EDGE,{"derivedFrom":makeQuery(id+"F1.opExtrude","CAP_EDGE",EDGE,{"disambiguationData":[OSD([sQuery(id+"F0.wireOp",EDGE,"E5.1.0.0")])],"isStart":true})}),-1.0]])]});
            var Q13;
            Q13=makeQuery(id+"F7.imprint","IMPRINT",FACE,{"disambiguationData":[TD([[makeQuery(id+"F7.imprint","IMPRINT",EDGE,{"derivedFrom":sQuery(id+"F7.wireOp",EDGE,"E118.bottom")}),-1.0]])]});
            var Q14;
            Q14=makeQuery(id+"F7.imprint","IMPRINT",FACE,{"disambiguationData":[TD([[makeQuery(id+"F7.imprint","IMPRINT",EDGE,{"derivedFrom":makeQuery(id+"F1.opExtrude","CAP_EDGE",EDGE,{"disambiguationData":[OSD([sQuery(id+"F0.wireOp",EDGE,"E5.4.0.0")])],"isStart":true})}),-1.0]])]});
            var Q15;
            Q15=makeQuery(id+"F7.imprint","IMPRINT",FACE,{"disambiguationData":[TD([[makeQuery(id+"F7.imprint","IMPRINT",EDGE,{"derivedFrom":sQuery(id+"F7.wireOp",EDGE,"E128.0")}),1.0]])]});
            var Q16;
            Q16=makeQuery(id+"F7.imprint","IMPRINT",FACE,{"disambiguationData":[TD([[makeQuery(id+"F7.imprint","IMPRINT",EDGE,{"derivedFrom":sQuery(id+"F7.wireOp",EDGE,"E145.bottom")}),-1.0]])]});
            var Q17;
            Q17=makeQuery(id+"F7.imprint","IMPRINT",FACE,{"disambiguationData":[TD([[makeQuery(id+"F7.imprint","IMPRINT",EDGE,{"derivedFrom":sQuery(id+"F7.wireOp",EDGE,"E152.bottom")}),-1.0]])]});
            extrude(context, id + "F8", {"entities" : qUnion([Q0, Q1, Q2, Q3, Q4, Q5, Q6, Q7, Q8, Q9, Q10, Q11, Q12, Q13, Q14, Q15, Q16, Q17]), "operationType" : NewBodyOperationType.ADD, "depth" : 2.54 * mm});
        }
        {
            var Q0;
            Q0=makeQuery(id+"F0.imprint","IMPRINT",FACE,{"disambiguationData":[TD([[makeQuery(id+"F0.imprint","IMPRINT",EDGE,{"derivedFrom":sQuery(id+"F0.wireOp",EDGE,"E6.4.0.0")}),1.0]])]});
            var Q1;
            Q1=makeQuery(id+"F0.imprint","IMPRINT",FACE,{"disambiguationData":[TD([[makeQuery(id+"F0.imprint","IMPRINT",EDGE,{"derivedFrom":sQuery(id+"F0.wireOp",EDGE,"E6.3.0.0")}),1.0]])]});
            var Q2;
            Q2=makeQuery(id+"F0.imprint","IMPRINT",FACE,{"disambiguationData":[TD([[makeQuery(id+"F0.imprint","IMPRINT",EDGE,{"derivedFrom":sQuery(id+"F0.wireOp",EDGE,"E6.2.0.0")}),1.0]])]});
            var Q3;
            Q3=makeQuery(id+"F0.imprint","IMPRINT",FACE,{"disambiguationData":[TD([[makeQuery(id+"F0.imprint","IMPRINT",EDGE,{"derivedFrom":sQuery(id+"F0.wireOp",EDGE,"E6.1.0.0")}),1.0]])]});
            var Q4;
            Q4=makeQuery(id+"F0.imprint","IMPRINT",FACE,{"disambiguationData":[TD([[makeQuery(id+"F0.imprint","IMPRINT",EDGE,{"derivedFrom":sQuery(id+"F0.wireOp",EDGE,"E3")}),1.0]])]});
            var Q5;
            Q5=makeQuery(id+"F0.imprint","IMPRINT",FACE,{"disambiguationData":[TD([[makeQuery(id+"F0.imprint","IMPRINT",EDGE,{"derivedFrom":sQuery(id+"F0.wireOp",EDGE,"E5.1.0.0")}),1.0]])]});
            var Q6;
            Q6=makeQuery(id+"F0.imprint","IMPRINT",FACE,{"disambiguationData":[TD([[makeQuery(id+"F0.imprint","IMPRINT",EDGE,{"derivedFrom":sQuery(id+"F0.wireOp",EDGE,"E5.2.0.0")}),1.0]])]});
            var Q7;
            Q7=makeQuery(id+"F0.imprint","IMPRINT",FACE,{"disambiguationData":[TD([[makeQuery(id+"F0.imprint","IMPRINT",EDGE,{"derivedFrom":sQuery(id+"F0.wireOp",EDGE,"E5.3.0.0")}),1.0]])]});
            var Q8;
            Q8=makeQuery(id+"F0.imprint","IMPRINT",FACE,{"disambiguationData":[TD([[makeQuery(id+"F0.imprint","IMPRINT",EDGE,{"derivedFrom":sQuery(id+"F0.wireOp",EDGE,"E5.4.0.0")}),1.0]])]});
            var Q9;
            Q9=makeQuery(id+"F0.imprint","IMPRINT",FACE,{"disambiguationData":[TD([[makeQuery(id+"F0.imprint","IMPRINT",EDGE,{"derivedFrom":sQuery(id+"F0.wireOp",EDGE,"E16")}),1.0]])]});
            var Q10;
            Q10=makeQuery(id+"F0.imprint","IMPRINT",FACE,{"disambiguationData":[TD([[makeQuery(id+"F0.imprint","IMPRINT",EDGE,{"derivedFrom":sQuery(id+"F0.wireOp",EDGE,"E17.1.0.0")}),1.0]])]});
            var Q11;
            Q11=makeQuery(id+"F0.imprint","IMPRINT",FACE,{"disambiguationData":[TD([[makeQuery(id+"F0.imprint","IMPRINT",EDGE,{"derivedFrom":sQuery(id+"F0.wireOp",EDGE,"E17.2.0.0")}),1.0]])]});
            var Q12;
            Q12=makeQuery(id+"F0.imprint","IMPRINT",FACE,{"disambiguationData":[TD([[makeQuery(id+"F0.imprint","IMPRINT",EDGE,{"derivedFrom":sQuery(id+"F0.wireOp",EDGE,"E17.3.0.0")}),1.0]])]});
            var Q13;
            Q13=makeQuery(id+"F0.imprint","IMPRINT",FACE,{"disambiguationData":[TD([[makeQuery(id+"F0.imprint","IMPRINT",EDGE,{"derivedFrom":sQuery(id+"F0.wireOp",EDGE,"E17.4.0.0")}),1.0]])]});
            var Q14;
            Q14=makeQuery(id+"F0.imprint","IMPRINT",FACE,{"disambiguationData":[TD([[makeQuery(id+"F0.imprint","IMPRINT",EDGE,{"derivedFrom":sQuery(id+"F0.wireOp",EDGE,"E17.5.0.0")}),1.0]])]});
            var Q15;
            Q15=makeQuery(id+"F0.imprint","IMPRINT",FACE,{"disambiguationData":[TD([[makeQuery(id+"F0.imprint","IMPRINT",EDGE,{"derivedFrom":sQuery(id+"F0.wireOp",EDGE,"E17.6.0.0")}),1.0]])]});
            var Q16;
            Q16=makeQuery(id+"F0.imprint","IMPRINT",FACE,{"disambiguationData":[TD([[makeQuery(id+"F0.imprint","IMPRINT",EDGE,{"derivedFrom":sQuery(id+"F0.wireOp",EDGE,"E17.7.0.0")}),1.0]])]});
            var Q17;
            Q17=makeQuery(id+"F0.imprint","IMPRINT",FACE,{"disambiguationData":[TD([[makeQuery(id+"F0.imprint","IMPRINT",EDGE,{"derivedFrom":sQuery(id+"F0.wireOp",EDGE,"E30")}),1.0]])]});
            var Q18;
            Q18=makeQuery(id+"F0.imprint","IMPRINT",FACE,{"disambiguationData":[TD([[makeQuery(id+"F0.imprint","IMPRINT",EDGE,{"derivedFrom":sQuery(id+"F0.wireOp",EDGE,"E28")}),1.0]])]});
            var Q19;
            Q19=makeQuery(id+"F0.imprint","IMPRINT",FACE,{"disambiguationData":[TD([[makeQuery(id+"F0.imprint","IMPRINT",EDGE,{"derivedFrom":sQuery(id+"F0.wireOp",EDGE,"E29")}),1.0]])]});
            var Q20;
            Q20=makeQuery(id+"F0.imprint","IMPRINT",FACE,{"disambiguationData":[TD([[makeQuery(id+"F0.imprint","IMPRINT",EDGE,{"derivedFrom":sQuery(id+"F0.wireOp",EDGE,"E27.3.0.0")}),1.0]])]});
            var Q21;
            Q21=makeQuery(id+"F0.imprint","IMPRINT",FACE,{"disambiguationData":[TD([[makeQuery(id+"F0.imprint","IMPRINT",EDGE,{"derivedFrom":sQuery(id+"F0.wireOp",EDGE,"E27.2.0.0")}),1.0]])]});
            var Q22;
            Q22=makeQuery(id+"F0.imprint","IMPRINT",FACE,{"disambiguationData":[TD([[makeQuery(id+"F0.imprint","IMPRINT",EDGE,{"derivedFrom":sQuery(id+"F0.wireOp",EDGE,"E27.1.0.0")}),1.0]])]});
            var Q23;
            Q23=makeQuery(id+"F0.imprint","IMPRINT",FACE,{"disambiguationData":[TD([[makeQuery(id+"F0.imprint","IMPRINT",EDGE,{"derivedFrom":sQuery(id+"F0.wireOp",EDGE,"E25")}),1.0]])]});
            var Q24;
            Q24=makeQuery(id+"F0.imprint","IMPRINT",FACE,{"disambiguationData":[TD([[makeQuery(id+"F0.imprint","IMPRINT",EDGE,{"derivedFrom":sQuery(id+"F0.wireOp",EDGE,"E26.1.0.0")}),1.0]])]});
            var Q25;
            Q25=makeQuery(id+"F0.imprint","IMPRINT",FACE,{"disambiguationData":[TD([[makeQuery(id+"F0.imprint","IMPRINT",EDGE,{"derivedFrom":sQuery(id+"F0.wireOp",EDGE,"E26.2.0.0")}),1.0]])]});
            var Q26;
            Q26=makeQuery(id+"F0.imprint","IMPRINT",FACE,{"disambiguationData":[TD([[makeQuery(id+"F0.imprint","IMPRINT",EDGE,{"derivedFrom":sQuery(id+"F0.wireOp",EDGE,"E26.3.0.0")}),1.0]])]});
            var Q27;
            Q27=makeQuery(id+"F0.imprint","IMPRINT",FACE,{"disambiguationData":[TD([[makeQuery(id+"F0.imprint","IMPRINT",EDGE,{"derivedFrom":sQuery(id+"F0.wireOp",EDGE,"E40.0.4.0")}),1.0]])]});
            var Q28;
            Q28=makeQuery(id+"F0.imprint","IMPRINT",FACE,{"disambiguationData":[TD([[makeQuery(id+"F0.imprint","IMPRINT",EDGE,{"derivedFrom":sQuery(id+"F0.wireOp",EDGE,"E40.0.3.0")}),1.0]])]});
            var Q29;
            Q29=makeQuery(id+"F0.imprint","IMPRINT",FACE,{"disambiguationData":[TD([[makeQuery(id+"F0.imprint","IMPRINT",EDGE,{"derivedFrom":sQuery(id+"F0.wireOp",EDGE,"E40.0.2.0")}),1.0]])]});
            var Q30;
            Q30=makeQuery(id+"F0.imprint","IMPRINT",FACE,{"disambiguationData":[TD([[makeQuery(id+"F0.imprint","IMPRINT",EDGE,{"derivedFrom":sQuery(id+"F0.wireOp",EDGE,"E40.0.1.0")}),1.0]])]});
            var Q31;
            Q31=makeQuery(id+"F0.imprint","IMPRINT",FACE,{"disambiguationData":[TD([[makeQuery(id+"F0.imprint","IMPRINT",EDGE,{"derivedFrom":sQuery(id+"F0.wireOp",EDGE,"E38")}),1.0]])]});
            var Q32;
            Q32=makeQuery(id+"F0.imprint","IMPRINT",FACE,{"disambiguationData":[TD([[makeQuery(id+"F0.imprint","IMPRINT",EDGE,{"derivedFrom":sQuery(id+"F0.wireOp",EDGE,"E39.0.1.0")}),1.0]])]});
            var Q33;
            Q33=makeQuery(id+"F0.imprint","IMPRINT",FACE,{"disambiguationData":[TD([[makeQuery(id+"F0.imprint","IMPRINT",EDGE,{"derivedFrom":sQuery(id+"F0.wireOp",EDGE,"E39.0.2.0")}),1.0]])]});
            var Q34;
            Q34=makeQuery(id+"F0.imprint","IMPRINT",FACE,{"disambiguationData":[TD([[makeQuery(id+"F0.imprint","IMPRINT",EDGE,{"derivedFrom":sQuery(id+"F0.wireOp",EDGE,"E39.0.3.0")}),1.0]])]});
            var Q35;
            Q35=makeQuery(id+"F0.imprint","IMPRINT",FACE,{"disambiguationData":[TD([[makeQuery(id+"F0.imprint","IMPRINT",EDGE,{"derivedFrom":sQuery(id+"F0.wireOp",EDGE,"E39.0.4.0")}),1.0]])]});
            var Q36;
            Q36=makeQuery(id+"F0.imprint","IMPRINT",FACE,{"disambiguationData":[TD([[makeQuery(id+"F0.imprint","IMPRINT",EDGE,{"derivedFrom":sQuery(id+"F0.wireOp",EDGE,"E60")}),1.0]])]});
            var Q37;
            Q37=makeQuery(id+"F0.imprint","IMPRINT",FACE,{"disambiguationData":[TD([[makeQuery(id+"F0.imprint","IMPRINT",EDGE,{"derivedFrom":sQuery(id+"F0.wireOp",EDGE,"E59")}),1.0]])]});
            var Q38;
            Q38=makeQuery(id+"F0.imprint","IMPRINT",FACE,{"disambiguationData":[TD([[makeQuery(id+"F0.imprint","IMPRINT",EDGE,{"derivedFrom":sQuery(id+"F0.wireOp",EDGE,"E58")}),1.0]])]});
            var Q39;
            Q39=makeQuery(id+"F0.imprint","IMPRINT",FACE,{"disambiguationData":[TD([[makeQuery(id+"F0.imprint","IMPRINT",EDGE,{"derivedFrom":sQuery(id+"F0.wireOp",EDGE,"E61")}),1.0]])]});
            var Q40;
            Q40=makeQuery(id+"F0.imprint","IMPRINT",FACE,{"disambiguationData":[TD([[makeQuery(id+"F0.imprint","IMPRINT",EDGE,{"derivedFrom":sQuery(id+"F0.wireOp",EDGE,"E62")}),1.0]])]});
            var Q41;
            Q41=makeQuery(id+"F0.imprint","IMPRINT",FACE,{"disambiguationData":[TD([[makeQuery(id+"F0.imprint","IMPRINT",EDGE,{"derivedFrom":sQuery(id+"F0.wireOp",EDGE,"E75.3.0.0")}),1.0]])]});
            var Q42;
            Q42=makeQuery(id+"F0.imprint","IMPRINT",FACE,{"disambiguationData":[TD([[makeQuery(id+"F0.imprint","IMPRINT",EDGE,{"derivedFrom":sQuery(id+"F0.wireOp",EDGE,"E75.2.0.0")}),1.0]])]});
            var Q43;
            Q43=makeQuery(id+"F0.imprint","IMPRINT",FACE,{"disambiguationData":[TD([[makeQuery(id+"F0.imprint","IMPRINT",EDGE,{"derivedFrom":sQuery(id+"F0.wireOp",EDGE,"E75.1.0.0")}),1.0]])]});
            var Q44;
            Q44=makeQuery(id+"F0.imprint","IMPRINT",FACE,{"disambiguationData":[TD([[makeQuery(id+"F0.imprint","IMPRINT",EDGE,{"derivedFrom":sQuery(id+"F0.wireOp",EDGE,"E74")}),1.0]])]});
            var Q45;
            Q45=makeQuery(id+"F0.imprint","IMPRINT",FACE,{"disambiguationData":[TD([[makeQuery(id+"F0.imprint","IMPRINT",EDGE,{"derivedFrom":sQuery(id+"F0.wireOp",EDGE,"E76.1.0.0")}),1.0]])]});
            var Q46;
            Q46=makeQuery(id+"F0.imprint","IMPRINT",FACE,{"disambiguationData":[TD([[makeQuery(id+"F0.imprint","IMPRINT",EDGE,{"derivedFrom":sQuery(id+"F0.wireOp",EDGE,"E76.2.0.0")}),1.0]])]});
            var Q47;
            Q47=makeQuery(id+"F0.imprint","IMPRINT",FACE,{"disambiguationData":[TD([[makeQuery(id+"F0.imprint","IMPRINT",EDGE,{"derivedFrom":sQuery(id+"F0.wireOp",EDGE,"E76.3.0.0")}),1.0]])]});
            var Q48;
            Q48=makeQuery(id+"F0.imprint","IMPRINT",FACE,{"disambiguationData":[TD([[makeQuery(id+"F0.imprint","IMPRINT",EDGE,{"derivedFrom":sQuery(id+"F0.wireOp",EDGE,"E90.0.3.0")}),1.0]])]});
            var Q49;
            Q49=makeQuery(id+"F0.imprint","IMPRINT",FACE,{"disambiguationData":[TD([[makeQuery(id+"F0.imprint","IMPRINT",EDGE,{"derivedFrom":sQuery(id+"F0.wireOp",EDGE,"E89.2.0.0")}),1.0]])]});
            var Q50;
            Q50=makeQuery(id+"F0.imprint","IMPRINT",FACE,{"disambiguationData":[TD([[makeQuery(id+"F0.imprint","IMPRINT",EDGE,{"derivedFrom":sQuery(id+"F0.wireOp",EDGE,"E89.1.0.0")}),1.0]])]});
            var Q51;
            Q51=makeQuery(id+"F0.imprint","IMPRINT",FACE,{"disambiguationData":[TD([[makeQuery(id+"F0.imprint","IMPRINT",EDGE,{"derivedFrom":sQuery(id+"F0.wireOp",EDGE,"E84")}),1.0]])]});
            var Q52;
            Q52=makeQuery(id+"F0.imprint","IMPRINT",FACE,{"disambiguationData":[TD([[makeQuery(id+"F0.imprint","IMPRINT",EDGE,{"derivedFrom":sQuery(id+"F0.wireOp",EDGE,"E86")}),1.0]])]});
            var Q53;
            Q53=makeQuery(id+"F0.imprint","IMPRINT",FACE,{"disambiguationData":[TD([[makeQuery(id+"F0.imprint","IMPRINT",EDGE,{"derivedFrom":sQuery(id+"F0.wireOp",EDGE,"E91.1.0.0")}),1.0]])]});
            var Q54;
            Q54=makeQuery(id+"F0.imprint","IMPRINT",FACE,{"disambiguationData":[TD([[makeQuery(id+"F0.imprint","IMPRINT",EDGE,{"derivedFrom":sQuery(id+"F0.wireOp",EDGE,"E91.2.0.0")}),1.0]])]});
            var Q55;
            Q55=makeQuery(id+"F0.imprint","IMPRINT",FACE,{"disambiguationData":[TD([[makeQuery(id+"F0.imprint","IMPRINT",EDGE,{"derivedFrom":sQuery(id+"F0.wireOp",EDGE,"E91.3.0.0")}),1.0]])]});
            extrude(context, id + "F9", {"entities" : qUnion([Q0, Q1, Q2, Q3, Q4, Q5, Q6, Q7, Q8, Q9, Q10, Q11, Q12, Q13, Q14, Q15, Q16, Q17, Q18, Q19, Q20, Q21, Q22, Q23, Q24, Q25, Q26, Q27, Q28, Q29, Q30, Q31, Q32, Q33, Q34, Q35, Q36, Q37, Q38, Q39, Q40, Q41, Q42, Q43, Q44, Q45, Q46, Q47, Q48, Q49, Q50, Q51, Q52, Q53, Q54, Q55]), "operationType" : NewBodyOperationType.ADD, "oppositeDirection" : true, "depth" : 8.25 * mm, "hasSecondDirection" : true, "secondDirectionOppositeDirection" : false, "secondDirectionDepth" : 3.17 * mm});
        }
        {
            var Q0;
            Q0=makeQuery(id+"F9.opExtrude","CAP_FACE",FACE,{"disambiguationData":[OSD([sQuery(id+"F0.wireOp",EDGE,"E60")])],"isStart":true});
            var Q1;
            Q1=makeQuery(id+"F9.opExtrude","CAP_FACE",FACE,{"disambiguationData":[OSD([sQuery(id+"F0.wireOp",EDGE,"E59")])],"isStart":true});
            var Q2;
            Q2=makeQuery(id+"F9.opExtrude","CAP_FACE",FACE,{"disambiguationData":[OSD([sQuery(id+"F0.wireOp",EDGE,"E58")])],"isStart":true});
            var Q3;
            Q3=makeQuery(id+"F9.opExtrude","CAP_FACE",FACE,{"disambiguationData":[OSD([sQuery(id+"F0.wireOp",EDGE,"E61")])],"isStart":true});
            var Q4;
            Q4=makeQuery(id+"F9.opExtrude","CAP_FACE",FACE,{"disambiguationData":[OSD([sQuery(id+"F0.wireOp",EDGE,"E62")])],"isStart":true});
            extrude(context, id + "F10", {"entities" : qUnion([Q0, Q1, Q2, Q3, Q4]), "operationType" : NewBodyOperationType.REMOVE, "oppositeDirection" : true, "depth" : 0.8 * mm});
        }
        {
            var Q0;
            {var subQ0=sQuery(id+"F0.wireOp",EDGE,"E39.0.1.0");Q0=makeQuery(id+"F9.boolean.opBoolean","SPLIT",FACE,{"disambiguationData":[TD([makeQuery(id+"F9.opExtrude","CAP_FACE",FACE,{"disambiguationData":[OSD([subQ0])],"isStart":true})])],"derivedFrom":makeQuery(id+"F9.opExtrude","SWEPT_FACE",FACE,{"disambiguationData":[OSD([subQ0])]})});}
            var Q1;
            {var subQ0=sQuery(id+"F0.wireOp",EDGE,"E39.0.2.0");Q1=makeQuery(id+"F9.boolean.opBoolean","SPLIT",FACE,{"disambiguationData":[TD([makeQuery(id+"F9.opExtrude","CAP_FACE",FACE,{"disambiguationData":[OSD([subQ0])],"isStart":true})])],"derivedFrom":makeQuery(id+"F9.opExtrude","SWEPT_FACE",FACE,{"disambiguationData":[OSD([subQ0])]})});}
            var Q2;
            {var subQ0=sQuery(id+"F0.wireOp",EDGE,"E39.0.3.0");Q2=makeQuery(id+"F9.boolean.opBoolean","SPLIT",FACE,{"disambiguationData":[TD([makeQuery(id+"F9.opExtrude","CAP_FACE",FACE,{"disambiguationData":[OSD([subQ0])],"isStart":true})])],"derivedFrom":makeQuery(id+"F9.opExtrude","SWEPT_FACE",FACE,{"disambiguationData":[OSD([subQ0])]})});}
            var Q3;
            {var subQ0=sQuery(id+"F0.wireOp",EDGE,"E39.0.4.0");Q3=makeQuery(id+"F9.boolean.opBoolean","SPLIT",FACE,{"disambiguationData":[TD([makeQuery(id+"F9.opExtrude","CAP_FACE",FACE,{"disambiguationData":[OSD([subQ0])],"isStart":true})])],"derivedFrom":makeQuery(id+"F9.opExtrude","SWEPT_FACE",FACE,{"disambiguationData":[OSD([subQ0])]})});}
            var Q4;
            {var subQ0=sQuery(id+"F0.wireOp",EDGE,"E38");Q4=makeQuery(id+"F9.boolean.opBoolean","SPLIT",FACE,{"disambiguationData":[TD([makeQuery(id+"F9.opExtrude","CAP_FACE",FACE,{"disambiguationData":[OSD([subQ0])],"isStart":true})])],"derivedFrom":makeQuery(id+"F9.opExtrude","SWEPT_FACE",FACE,{"disambiguationData":[OSD([subQ0])]})});}
            var Q5;
            {var subQ0=sQuery(id+"F0.wireOp",EDGE,"E40.0.1.0");Q5=makeQuery(id+"F9.boolean.opBoolean","SPLIT",FACE,{"disambiguationData":[TD([makeQuery(id+"F9.opExtrude","CAP_FACE",FACE,{"disambiguationData":[OSD([subQ0])],"isStart":true})])],"derivedFrom":makeQuery(id+"F9.opExtrude","SWEPT_FACE",FACE,{"disambiguationData":[OSD([subQ0])]})});}
            var Q6;
            {var subQ0=sQuery(id+"F0.wireOp",EDGE,"E40.0.2.0");Q6=makeQuery(id+"F9.boolean.opBoolean","SPLIT",FACE,{"disambiguationData":[TD([makeQuery(id+"F9.opExtrude","CAP_FACE",FACE,{"disambiguationData":[OSD([subQ0])],"isStart":true})])],"derivedFrom":makeQuery(id+"F9.opExtrude","SWEPT_FACE",FACE,{"disambiguationData":[OSD([subQ0])]})});}
            var Q7;
            {var subQ0=sQuery(id+"F0.wireOp",EDGE,"E40.0.3.0");Q7=makeQuery(id+"F9.boolean.opBoolean","SPLIT",FACE,{"disambiguationData":[TD([makeQuery(id+"F9.opExtrude","CAP_FACE",FACE,{"disambiguationData":[OSD([subQ0])],"isStart":true})])],"derivedFrom":makeQuery(id+"F9.opExtrude","SWEPT_FACE",FACE,{"disambiguationData":[OSD([subQ0])]})});}
            var Q8;
            {var subQ0=sQuery(id+"F0.wireOp",EDGE,"E40.0.4.0");Q8=makeQuery(id+"F9.boolean.opBoolean","SPLIT",FACE,{"disambiguationData":[TD([makeQuery(id+"F9.opExtrude","CAP_FACE",FACE,{"disambiguationData":[OSD([subQ0])],"isStart":true})])],"derivedFrom":makeQuery(id+"F9.opExtrude","SWEPT_FACE",FACE,{"disambiguationData":[OSD([subQ0])]})});}
            var Q9;
            {var subQ0=sQuery(id+"F0.wireOp",EDGE,"E26.3.0.0");Q9=makeQuery(id+"F9.boolean.opBoolean","SPLIT",FACE,{"disambiguationData":[TD([makeQuery(id+"F9.opExtrude","CAP_FACE",FACE,{"disambiguationData":[OSD([subQ0])],"isStart":true})])],"derivedFrom":makeQuery(id+"F9.opExtrude","SWEPT_FACE",FACE,{"disambiguationData":[OSD([subQ0])]})});}
            var Q10;
            {var subQ0=sQuery(id+"F0.wireOp",EDGE,"E26.2.0.0");Q10=makeQuery(id+"F9.boolean.opBoolean","SPLIT",FACE,{"disambiguationData":[TD([makeQuery(id+"F9.opExtrude","CAP_FACE",FACE,{"disambiguationData":[OSD([subQ0])],"isStart":true})])],"derivedFrom":makeQuery(id+"F9.opExtrude","SWEPT_FACE",FACE,{"disambiguationData":[OSD([subQ0])]})});}
            var Q11;
            {var subQ0=sQuery(id+"F0.wireOp",EDGE,"E26.1.0.0");Q11=makeQuery(id+"F9.boolean.opBoolean","SPLIT",FACE,{"disambiguationData":[TD([makeQuery(id+"F9.opExtrude","CAP_FACE",FACE,{"disambiguationData":[OSD([subQ0])],"isStart":true})])],"derivedFrom":makeQuery(id+"F9.opExtrude","SWEPT_FACE",FACE,{"disambiguationData":[OSD([subQ0])]})});}
            var Q12;
            {var subQ0=sQuery(id+"F0.wireOp",EDGE,"E25");Q12=makeQuery(id+"F9.boolean.opBoolean","SPLIT",FACE,{"disambiguationData":[TD([makeQuery(id+"F9.opExtrude","CAP_FACE",FACE,{"disambiguationData":[OSD([subQ0])],"isStart":true})])],"derivedFrom":makeQuery(id+"F9.opExtrude","SWEPT_FACE",FACE,{"disambiguationData":[OSD([subQ0])]})});}
            var Q13;
            {var subQ0=sQuery(id+"F0.wireOp",EDGE,"E27.1.0.0");Q13=makeQuery(id+"F9.boolean.opBoolean","SPLIT",FACE,{"disambiguationData":[TD([makeQuery(id+"F9.opExtrude","CAP_FACE",FACE,{"disambiguationData":[OSD([subQ0])],"isStart":true})])],"derivedFrom":makeQuery(id+"F9.opExtrude","SWEPT_FACE",FACE,{"disambiguationData":[OSD([subQ0])]})});}
            var Q14;
            {var subQ0=sQuery(id+"F0.wireOp",EDGE,"E27.2.0.0");Q14=makeQuery(id+"F9.boolean.opBoolean","SPLIT",FACE,{"disambiguationData":[TD([makeQuery(id+"F9.opExtrude","CAP_FACE",FACE,{"disambiguationData":[OSD([subQ0])],"isStart":true})])],"derivedFrom":makeQuery(id+"F9.opExtrude","SWEPT_FACE",FACE,{"disambiguationData":[OSD([subQ0])]})});}
            var Q15;
            {var subQ0=sQuery(id+"F0.wireOp",EDGE,"E27.3.0.0");Q15=makeQuery(id+"F9.boolean.opBoolean","SPLIT",FACE,{"disambiguationData":[TD([makeQuery(id+"F9.opExtrude","CAP_FACE",FACE,{"disambiguationData":[OSD([subQ0])],"isStart":true})])],"derivedFrom":makeQuery(id+"F9.opExtrude","SWEPT_FACE",FACE,{"disambiguationData":[OSD([subQ0])]})});}
            var Q16;
            {var subQ0=sQuery(id+"F0.wireOp",EDGE,"E16");Q16=makeQuery(id+"F9.boolean.opBoolean","SPLIT",FACE,{"disambiguationData":[TD([makeQuery(id+"F9.opExtrude","CAP_FACE",FACE,{"disambiguationData":[OSD([subQ0])],"isStart":true})])],"derivedFrom":makeQuery(id+"F9.opExtrude","SWEPT_FACE",FACE,{"disambiguationData":[OSD([subQ0])]})});}
            var Q17;
            {var subQ0=sQuery(id+"F0.wireOp",EDGE,"E17.1.0.0");Q17=makeQuery(id+"F9.boolean.opBoolean","SPLIT",FACE,{"disambiguationData":[TD([makeQuery(id+"F9.opExtrude","CAP_FACE",FACE,{"disambiguationData":[OSD([subQ0])],"isStart":true})])],"derivedFrom":makeQuery(id+"F9.opExtrude","SWEPT_FACE",FACE,{"disambiguationData":[OSD([subQ0])]})});}
            var Q18;
            {var subQ0=sQuery(id+"F0.wireOp",EDGE,"E17.3.0.0");Q18=makeQuery(id+"F9.boolean.opBoolean","SPLIT",FACE,{"disambiguationData":[TD([makeQuery(id+"F9.opExtrude","CAP_FACE",FACE,{"disambiguationData":[OSD([subQ0])],"isStart":true})])],"derivedFrom":makeQuery(id+"F9.opExtrude","SWEPT_FACE",FACE,{"disambiguationData":[OSD([subQ0])]})});}
            var Q19;
            {var subQ0=sQuery(id+"F0.wireOp",EDGE,"E17.2.0.0");Q19=makeQuery(id+"F9.boolean.opBoolean","SPLIT",FACE,{"disambiguationData":[TD([makeQuery(id+"F9.opExtrude","CAP_FACE",FACE,{"disambiguationData":[OSD([subQ0])],"isStart":true})])],"derivedFrom":makeQuery(id+"F9.opExtrude","SWEPT_FACE",FACE,{"disambiguationData":[OSD([subQ0])]})});}
            var Q20;
            {var subQ0=sQuery(id+"F0.wireOp",EDGE,"E17.4.0.0");Q20=makeQuery(id+"F9.boolean.opBoolean","SPLIT",FACE,{"disambiguationData":[TD([makeQuery(id+"F9.opExtrude","CAP_FACE",FACE,{"disambiguationData":[OSD([subQ0])],"isStart":true})])],"derivedFrom":makeQuery(id+"F9.opExtrude","SWEPT_FACE",FACE,{"disambiguationData":[OSD([subQ0])]})});}
            var Q21;
            {var subQ0=sQuery(id+"F0.wireOp",EDGE,"E17.5.0.0");Q21=makeQuery(id+"F9.boolean.opBoolean","SPLIT",FACE,{"disambiguationData":[TD([makeQuery(id+"F9.opExtrude","CAP_FACE",FACE,{"disambiguationData":[OSD([subQ0])],"isStart":true})])],"derivedFrom":makeQuery(id+"F9.opExtrude","SWEPT_FACE",FACE,{"disambiguationData":[OSD([subQ0])]})});}
            var Q22;
            {var subQ0=sQuery(id+"F0.wireOp",EDGE,"E17.6.0.0");Q22=makeQuery(id+"F9.boolean.opBoolean","SPLIT",FACE,{"disambiguationData":[TD([makeQuery(id+"F9.opExtrude","CAP_FACE",FACE,{"disambiguationData":[OSD([subQ0])],"isStart":true})])],"derivedFrom":makeQuery(id+"F9.opExtrude","SWEPT_FACE",FACE,{"disambiguationData":[OSD([subQ0])]})});}
            var Q23;
            {var subQ0=sQuery(id+"F0.wireOp",EDGE,"E17.7.0.0");Q23=makeQuery(id+"F9.boolean.opBoolean","SPLIT",FACE,{"disambiguationData":[TD([makeQuery(id+"F9.opExtrude","CAP_FACE",FACE,{"disambiguationData":[OSD([subQ0])],"isStart":true})])],"derivedFrom":makeQuery(id+"F9.opExtrude","SWEPT_FACE",FACE,{"disambiguationData":[OSD([subQ0])]})});}
            var Q24;
            {var subQ0=sQuery(id+"F0.wireOp",EDGE,"E30");Q24=makeQuery(id+"F9.boolean.opBoolean","SPLIT",FACE,{"disambiguationData":[TD([makeQuery(id+"F9.opExtrude","CAP_FACE",FACE,{"disambiguationData":[OSD([subQ0])],"isStart":true})])],"derivedFrom":makeQuery(id+"F9.opExtrude","SWEPT_FACE",FACE,{"disambiguationData":[OSD([subQ0])]})});}
            var Q25;
            {var subQ0=sQuery(id+"F0.wireOp",EDGE,"E28");Q25=makeQuery(id+"F9.boolean.opBoolean","SPLIT",FACE,{"disambiguationData":[TD([makeQuery(id+"F9.opExtrude","CAP_FACE",FACE,{"disambiguationData":[OSD([subQ0])],"isStart":true})])],"derivedFrom":makeQuery(id+"F9.opExtrude","SWEPT_FACE",FACE,{"disambiguationData":[OSD([subQ0])]})});}
            var Q26;
            {var subQ0=sQuery(id+"F0.wireOp",EDGE,"E29");Q26=makeQuery(id+"F9.boolean.opBoolean","SPLIT",FACE,{"disambiguationData":[TD([makeQuery(id+"F9.opExtrude","CAP_FACE",FACE,{"disambiguationData":[OSD([subQ0])],"isStart":true})])],"derivedFrom":makeQuery(id+"F9.opExtrude","SWEPT_FACE",FACE,{"disambiguationData":[OSD([subQ0])]})});}
            var Q27;
            {var subQ0=sQuery(id+"F0.wireOp",EDGE,"E6.4.0.0");Q27=makeQuery(id+"F9.boolean.opBoolean","SPLIT",FACE,{"disambiguationData":[TD([makeQuery(id+"F9.opExtrude","CAP_FACE",FACE,{"disambiguationData":[OSD([subQ0])],"isStart":true})])],"derivedFrom":makeQuery(id+"F9.opExtrude","SWEPT_FACE",FACE,{"disambiguationData":[OSD([subQ0])]})});}
            var Q28;
            {var subQ0=sQuery(id+"F0.wireOp",EDGE,"E6.3.0.0");Q28=makeQuery(id+"F9.boolean.opBoolean","SPLIT",FACE,{"disambiguationData":[TD([makeQuery(id+"F9.opExtrude","CAP_FACE",FACE,{"disambiguationData":[OSD([subQ0])],"isStart":true})])],"derivedFrom":makeQuery(id+"F9.opExtrude","SWEPT_FACE",FACE,{"disambiguationData":[OSD([subQ0])]})});}
            var Q29;
            {var subQ0=sQuery(id+"F0.wireOp",EDGE,"E6.2.0.0");Q29=makeQuery(id+"F9.boolean.opBoolean","SPLIT",FACE,{"disambiguationData":[TD([makeQuery(id+"F9.opExtrude","CAP_FACE",FACE,{"disambiguationData":[OSD([subQ0])],"isStart":true})])],"derivedFrom":makeQuery(id+"F9.opExtrude","SWEPT_FACE",FACE,{"disambiguationData":[OSD([subQ0])]})});}
            var Q30;
            {var subQ0=sQuery(id+"F0.wireOp",EDGE,"E6.1.0.0");Q30=makeQuery(id+"F9.boolean.opBoolean","SPLIT",FACE,{"disambiguationData":[TD([makeQuery(id+"F9.opExtrude","CAP_FACE",FACE,{"disambiguationData":[OSD([subQ0])],"isStart":true})])],"derivedFrom":makeQuery(id+"F9.opExtrude","SWEPT_FACE",FACE,{"disambiguationData":[OSD([subQ0])]})});}
            var Q31;
            {var subQ0=sQuery(id+"F0.wireOp",EDGE,"E3");Q31=makeQuery(id+"F9.boolean.opBoolean","SPLIT",FACE,{"disambiguationData":[TD([makeQuery(id+"F9.opExtrude","CAP_FACE",FACE,{"disambiguationData":[OSD([subQ0])],"isStart":true})])],"derivedFrom":makeQuery(id+"F9.opExtrude","SWEPT_FACE",FACE,{"disambiguationData":[OSD([subQ0])]})});}
            var Q32;
            {var subQ0=sQuery(id+"F0.wireOp",EDGE,"E5.1.0.0");Q32=makeQuery(id+"F9.boolean.opBoolean","SPLIT",FACE,{"disambiguationData":[TD([makeQuery(id+"F9.opExtrude","CAP_FACE",FACE,{"disambiguationData":[OSD([subQ0])],"isStart":true})])],"derivedFrom":makeQuery(id+"F9.opExtrude","SWEPT_FACE",FACE,{"disambiguationData":[OSD([subQ0])]})});}
            var Q33;
            {var subQ0=sQuery(id+"F0.wireOp",EDGE,"E5.2.0.0");Q33=makeQuery(id+"F9.boolean.opBoolean","SPLIT",FACE,{"disambiguationData":[TD([makeQuery(id+"F9.opExtrude","CAP_FACE",FACE,{"disambiguationData":[OSD([subQ0])],"isStart":true})])],"derivedFrom":makeQuery(id+"F9.opExtrude","SWEPT_FACE",FACE,{"disambiguationData":[OSD([subQ0])]})});}
            var Q34;
            {var subQ0=sQuery(id+"F0.wireOp",EDGE,"E5.3.0.0");Q34=makeQuery(id+"F9.boolean.opBoolean","SPLIT",FACE,{"disambiguationData":[TD([makeQuery(id+"F9.opExtrude","CAP_FACE",FACE,{"disambiguationData":[OSD([subQ0])],"isStart":true})])],"derivedFrom":makeQuery(id+"F9.opExtrude","SWEPT_FACE",FACE,{"disambiguationData":[OSD([subQ0])]})});}
            var Q35;
            {var subQ0=sQuery(id+"F0.wireOp",EDGE,"E5.4.0.0");Q35=makeQuery(id+"F9.boolean.opBoolean","SPLIT",FACE,{"disambiguationData":[TD([makeQuery(id+"F9.opExtrude","CAP_FACE",FACE,{"disambiguationData":[OSD([subQ0])],"isStart":true})])],"derivedFrom":makeQuery(id+"F9.opExtrude","SWEPT_FACE",FACE,{"disambiguationData":[OSD([subQ0])]})});}
            var Q36;
            {var subQ0=sQuery(id+"F0.wireOp",EDGE,"E60");Q36=makeQuery(id+"F9.boolean.opBoolean","SPLIT",FACE,{"disambiguationData":[TD([makeQuery(id+"F9.opExtrude","CAP_FACE",FACE,{"disambiguationData":[OSD([subQ0])],"isStart":true})])],"derivedFrom":makeQuery(id+"F9.opExtrude","SWEPT_FACE",FACE,{"disambiguationData":[OSD([subQ0])]})});}
            var Q37;
            {var subQ0=sQuery(id+"F0.wireOp",EDGE,"E59");Q37=makeQuery(id+"F9.boolean.opBoolean","SPLIT",FACE,{"disambiguationData":[TD([makeQuery(id+"F9.opExtrude","CAP_FACE",FACE,{"disambiguationData":[OSD([subQ0])],"isStart":true})])],"derivedFrom":makeQuery(id+"F9.opExtrude","SWEPT_FACE",FACE,{"disambiguationData":[OSD([subQ0])]})});}
            var Q38;
            {var subQ0=sQuery(id+"F0.wireOp",EDGE,"E58");Q38=makeQuery(id+"F9.boolean.opBoolean","SPLIT",FACE,{"disambiguationData":[TD([makeQuery(id+"F9.opExtrude","CAP_FACE",FACE,{"disambiguationData":[OSD([subQ0])],"isStart":true})])],"derivedFrom":makeQuery(id+"F9.opExtrude","SWEPT_FACE",FACE,{"disambiguationData":[OSD([subQ0])]})});}
            var Q39;
            {var subQ0=sQuery(id+"F0.wireOp",EDGE,"E61");Q39=makeQuery(id+"F9.boolean.opBoolean","SPLIT",FACE,{"disambiguationData":[TD([makeQuery(id+"F9.opExtrude","CAP_FACE",FACE,{"disambiguationData":[OSD([subQ0])],"isStart":true})])],"derivedFrom":makeQuery(id+"F9.opExtrude","SWEPT_FACE",FACE,{"disambiguationData":[OSD([subQ0])]})});}
            var Q40;
            {var subQ0=sQuery(id+"F0.wireOp",EDGE,"E62");Q40=makeQuery(id+"F9.boolean.opBoolean","SPLIT",FACE,{"disambiguationData":[TD([makeQuery(id+"F9.opExtrude","CAP_FACE",FACE,{"disambiguationData":[OSD([subQ0])],"isStart":true})])],"derivedFrom":makeQuery(id+"F9.opExtrude","SWEPT_FACE",FACE,{"disambiguationData":[OSD([subQ0])]})});}
            var Q41;
            {var subQ0=sQuery(id+"F0.wireOp",EDGE,"E74");Q41=makeQuery(id+"F9.boolean.opBoolean","SPLIT",FACE,{"disambiguationData":[TD([makeQuery(id+"F9.opExtrude","CAP_FACE",FACE,{"disambiguationData":[OSD([subQ0])],"isStart":true})])],"derivedFrom":makeQuery(id+"F9.opExtrude","SWEPT_FACE",FACE,{"disambiguationData":[OSD([subQ0])]})});}
            var Q42;
            {var subQ0=sQuery(id+"F0.wireOp",EDGE,"E76.1.0.0");Q42=makeQuery(id+"F9.boolean.opBoolean","SPLIT",FACE,{"disambiguationData":[TD([makeQuery(id+"F9.opExtrude","CAP_FACE",FACE,{"disambiguationData":[OSD([subQ0])],"isStart":true})])],"derivedFrom":makeQuery(id+"F9.opExtrude","SWEPT_FACE",FACE,{"disambiguationData":[OSD([subQ0])]})});}
            var Q43;
            {var subQ0=sQuery(id+"F0.wireOp",EDGE,"E76.2.0.0");Q43=makeQuery(id+"F9.boolean.opBoolean","SPLIT",FACE,{"disambiguationData":[TD([makeQuery(id+"F9.opExtrude","CAP_FACE",FACE,{"disambiguationData":[OSD([subQ0])],"isStart":true})])],"derivedFrom":makeQuery(id+"F9.opExtrude","SWEPT_FACE",FACE,{"disambiguationData":[OSD([subQ0])]})});}
            var Q44;
            {var subQ0=sQuery(id+"F0.wireOp",EDGE,"E75.1.0.0");Q44=makeQuery(id+"F9.boolean.opBoolean","SPLIT",FACE,{"disambiguationData":[TD([makeQuery(id+"F9.opExtrude","CAP_FACE",FACE,{"disambiguationData":[OSD([subQ0])],"isStart":true})])],"derivedFrom":makeQuery(id+"F9.opExtrude","SWEPT_FACE",FACE,{"disambiguationData":[OSD([subQ0])]})});}
            var Q45;
            {var subQ0=sQuery(id+"F0.wireOp",EDGE,"E75.2.0.0");Q45=makeQuery(id+"F9.boolean.opBoolean","SPLIT",FACE,{"disambiguationData":[TD([makeQuery(id+"F9.opExtrude","CAP_FACE",FACE,{"disambiguationData":[OSD([subQ0])],"isStart":true})])],"derivedFrom":makeQuery(id+"F9.opExtrude","SWEPT_FACE",FACE,{"disambiguationData":[OSD([subQ0])]})});}
            var Q46;
            {var subQ0=sQuery(id+"F0.wireOp",EDGE,"E75.3.0.0");Q46=makeQuery(id+"F9.boolean.opBoolean","SPLIT",FACE,{"disambiguationData":[TD([makeQuery(id+"F9.opExtrude","CAP_FACE",FACE,{"disambiguationData":[OSD([subQ0])],"isStart":true})])],"derivedFrom":makeQuery(id+"F9.opExtrude","SWEPT_FACE",FACE,{"disambiguationData":[OSD([subQ0])]})});}
            var Q47;
            {var subQ0=sQuery(id+"F0.wireOp",EDGE,"E76.3.0.0");Q47=makeQuery(id+"F9.boolean.opBoolean","SPLIT",FACE,{"disambiguationData":[TD([makeQuery(id+"F9.opExtrude","CAP_FACE",FACE,{"disambiguationData":[OSD([subQ0])],"isStart":true})])],"derivedFrom":makeQuery(id+"F9.opExtrude","SWEPT_FACE",FACE,{"disambiguationData":[OSD([subQ0])]})});}
            var Q48;
            {var subQ0=sQuery(id+"F0.wireOp",EDGE,"E91.3.0.0");Q48=makeQuery(id+"F9.boolean.opBoolean","SPLIT",FACE,{"disambiguationData":[TD([makeQuery(id+"F9.opExtrude","CAP_FACE",FACE,{"disambiguationData":[OSD([subQ0])],"isStart":true})])],"derivedFrom":makeQuery(id+"F9.opExtrude","SWEPT_FACE",FACE,{"disambiguationData":[OSD([subQ0])]})});}
            var Q49;
            {var subQ0=sQuery(id+"F0.wireOp",EDGE,"E91.2.0.0");Q49=makeQuery(id+"F9.boolean.opBoolean","SPLIT",FACE,{"disambiguationData":[TD([makeQuery(id+"F9.opExtrude","CAP_FACE",FACE,{"disambiguationData":[OSD([subQ0])],"isStart":true})])],"derivedFrom":makeQuery(id+"F9.opExtrude","SWEPT_FACE",FACE,{"disambiguationData":[OSD([subQ0])]})});}
            var Q50;
            {var subQ0=sQuery(id+"F0.wireOp",EDGE,"E91.1.0.0");Q50=makeQuery(id+"F9.boolean.opBoolean","SPLIT",FACE,{"disambiguationData":[TD([makeQuery(id+"F9.opExtrude","CAP_FACE",FACE,{"disambiguationData":[OSD([subQ0])],"isStart":true})])],"derivedFrom":makeQuery(id+"F9.opExtrude","SWEPT_FACE",FACE,{"disambiguationData":[OSD([subQ0])]})});}
            var Q51;
            {var subQ0=sQuery(id+"F0.wireOp",EDGE,"E86");Q51=makeQuery(id+"F9.boolean.opBoolean","SPLIT",FACE,{"disambiguationData":[TD([makeQuery(id+"F9.opExtrude","CAP_FACE",FACE,{"disambiguationData":[OSD([subQ0])],"isStart":true})])],"derivedFrom":makeQuery(id+"F9.opExtrude","SWEPT_FACE",FACE,{"disambiguationData":[OSD([subQ0])]})});}
            var Q52;
            {var subQ0=sQuery(id+"F0.wireOp",EDGE,"E84");Q52=makeQuery(id+"F9.boolean.opBoolean","SPLIT",FACE,{"disambiguationData":[TD([makeQuery(id+"F9.opExtrude","CAP_FACE",FACE,{"disambiguationData":[OSD([subQ0])],"isStart":true})])],"derivedFrom":makeQuery(id+"F9.opExtrude","SWEPT_FACE",FACE,{"disambiguationData":[OSD([subQ0])]})});}
            var Q53;
            {var subQ0=sQuery(id+"F0.wireOp",EDGE,"E89.1.0.0");Q53=makeQuery(id+"F9.boolean.opBoolean","SPLIT",FACE,{"disambiguationData":[TD([makeQuery(id+"F9.opExtrude","CAP_FACE",FACE,{"disambiguationData":[OSD([subQ0])],"isStart":true})])],"derivedFrom":makeQuery(id+"F9.opExtrude","SWEPT_FACE",FACE,{"disambiguationData":[OSD([subQ0])]})});}
            var Q54;
            {var subQ0=sQuery(id+"F0.wireOp",EDGE,"E89.2.0.0");Q54=makeQuery(id+"F9.boolean.opBoolean","SPLIT",FACE,{"disambiguationData":[TD([makeQuery(id+"F9.opExtrude","CAP_FACE",FACE,{"disambiguationData":[OSD([subQ0])],"isStart":true})])],"derivedFrom":makeQuery(id+"F9.opExtrude","SWEPT_FACE",FACE,{"disambiguationData":[OSD([subQ0])]})});}
            var Q55;
            {var subQ0=sQuery(id+"F0.wireOp",EDGE,"E90.0.3.0");Q55=makeQuery(id+"F9.boolean.opBoolean","SPLIT",FACE,{"disambiguationData":[TD([makeQuery(id+"F9.opExtrude","CAP_FACE",FACE,{"disambiguationData":[OSD([subQ0])],"isStart":true})])],"derivedFrom":makeQuery(id+"F9.opExtrude","SWEPT_FACE",FACE,{"disambiguationData":[OSD([subQ0])]})});}
            fillet(context, id + "F11", {"entities" : qUnion([Q0, Q1, Q2, Q3, Q4, Q5, Q6, Q7, Q8, Q9, Q10, Q11, Q12, Q13, Q14, Q15, Q16, Q17, Q18, Q19, Q20, Q21, Q22, Q23, Q24, Q25, Q26, Q27, Q28, Q29, Q30, Q31, Q32, Q33, Q34, Q35, Q36, Q37, Q38, Q39, Q40, Q41, Q42, Q43, Q44, Q45, Q46, Q47, Q48, Q49, Q50, Q51, Q52, Q53, Q54, Q55]), "radius" : 0.5 * mm, "tangentPropagation" : true, "allowEdgeOverflow" : false});
        }
        {
            var Q0;
            Q0=makeQuery(id+"F1.opExtrude","CAP_FACE",FACE,{"disambiguationData":[OSD([sQuery(id+"F0.wireOp",EDGE,"E31.bottom"),sQuery(id+"F0.wireOp",EDGE,"E31.top"),sQuery(id+"F0.wireOp",EDGE,"E31.left"),sQuery(id+"F0.wireOp",EDGE,"E31.right"),sQuery(id+"F0.wireOp",EDGE,"E32.filletArc"),sQuery(id+"F0.wireOp",EDGE,"E33.filletArc"),sQuery(id+"F0.wireOp",EDGE,"E34.filletArc"),sQuery(id+"F0.wireOp",EDGE,"E35.filletArc"),sQuery(id+"F0.wireOp",EDGE,"E36"),sQuery(id+"F0.wireOp",EDGE,"E37"),sQuery(id+"F0.wireOp",EDGE,"E38"),sQuery(id+"F0.wireOp",EDGE,"E39.0.1.0"),sQuery(id+"F0.wireOp",EDGE,"E39.0.2.0"),sQuery(id+"F0.wireOp",EDGE,"E39.0.3.0"),sQuery(id+"F0.wireOp",EDGE,"E39.0.4.0"),sQuery(id+"F0.wireOp",EDGE,"E40.0.1.0"),sQuery(id+"F0.wireOp",EDGE,"E40.0.2.0"),sQuery(id+"F0.wireOp",EDGE,"E40.0.3.0"),sQuery(id+"F0.wireOp",EDGE,"E40.0.4.0"),sQuery(id+"F0.wireOp",EDGE,"E41"),sQuery(id+"F0.wireOp",EDGE,"E42.0.1.0"),sQuery(id+"F0.wireOp",EDGE,"E42.1.0.0"),sQuery(id+"F0.wireOp",EDGE,"E42.1.1.0"),sQuery(id+"F0.wireOp",EDGE,"E42.2.0.0"),sQuery(id+"F0.wireOp",EDGE,"E42.2.1.0"),sQuery(id+"F0.wireOp",EDGE,"E42.3.0.0"),sQuery(id+"F0.wireOp",EDGE,"E42.3.1.0"),sQuery(id+"F0.wireOp",EDGE,"E45"),sQuery(id+"F0.wireOp",EDGE,"E46"),sQuery(id+"F0.wireOp",EDGE,"E47"),sQuery(id+"F0.wireOp",EDGE,"E48")])],"isStart":false});
            var sketch = newSketch(context, id + "F12", { "sketchPlane" : qUnion([Q0])});
            skLineSegment(sketch, "E153", {"start": v(11.43, -30.48) * mm, "end": v(11.43, -33.02) * mm});
            skLineSegment(sketch, "E154", {"start": v(12.45, -30.48) * mm, "end": v(12.45, -33.02) * mm});
            skSolve(sketch);
        }
        {
            var Q0;
            {var subQ0=sQuery(id+"F12.wireOp",EDGE,"E153");Q0=makeQuery(id+"F12.imprint","IMPRINT",FACE,{"disambiguationData":[TD([[makeQuery(id+"F12.imprint","IMPRINT",EDGE,{"derivedFrom":subQ0}),1.0]])]});}
            var Q1;
            {var subQ0=makeQuery(id+"F1.opExtrude","CAP_EDGE",EDGE,{"disambiguationData":[OSD([sQuery(id+"F0.wireOp",EDGE,"E42.1.1.0")])],"isStart":false});var subQ1=makeQuery(id+"F12.imprint","INTERSECT",VERTEX,{"derivedFrom":[subQ0,sQuery(id+"F12.wireOp",EDGE,"E153")]});Q1=makeQuery(id+"F12.imprint","IMPRINT",FACE,{"disambiguationData":[TD([[makeQuery(id+"F12.imprint","IMPRINT",EDGE,{"disambiguationData":[TD([[subQ1,-1.0]])],"derivedFrom":subQ0}),1.0]])]});}
            var Q2;
            {var subQ0=makeQuery(id+"F1.opExtrude","CAP_EDGE",EDGE,{"disambiguationData":[OSD([sQuery(id+"F0.wireOp",EDGE,"E42.1.0.0")])],"isStart":false});var subQ1=makeQuery(id+"F12.imprint","INTERSECT",VERTEX,{"derivedFrom":[subQ0,sQuery(id+"F12.wireOp",EDGE,"E153")]});Q2=makeQuery(id+"F12.imprint","IMPRINT",FACE,{"disambiguationData":[TD([[makeQuery(id+"F12.imprint","IMPRINT",EDGE,{"disambiguationData":[TD([[subQ1,1.0]])],"derivedFrom":subQ0}),1.0]])]});}
            var Q3;
            Q3=makeQuery(id+"F1.opExtrude","CAP_FACE",FACE,{"disambiguationData":[OSD([sQuery(id+"F0.wireOp",EDGE,"E31.bottom"),sQuery(id+"F0.wireOp",EDGE,"E31.top"),sQuery(id+"F0.wireOp",EDGE,"E31.left"),sQuery(id+"F0.wireOp",EDGE,"E31.right"),sQuery(id+"F0.wireOp",EDGE,"E32.filletArc"),sQuery(id+"F0.wireOp",EDGE,"E33.filletArc"),sQuery(id+"F0.wireOp",EDGE,"E34.filletArc"),sQuery(id+"F0.wireOp",EDGE,"E35.filletArc"),sQuery(id+"F0.wireOp",EDGE,"E36"),sQuery(id+"F0.wireOp",EDGE,"E37"),sQuery(id+"F0.wireOp",EDGE,"E38"),sQuery(id+"F0.wireOp",EDGE,"E39.0.1.0"),sQuery(id+"F0.wireOp",EDGE,"E39.0.2.0"),sQuery(id+"F0.wireOp",EDGE,"E39.0.3.0"),sQuery(id+"F0.wireOp",EDGE,"E39.0.4.0"),sQuery(id+"F0.wireOp",EDGE,"E40.0.1.0"),sQuery(id+"F0.wireOp",EDGE,"E40.0.2.0"),sQuery(id+"F0.wireOp",EDGE,"E40.0.3.0"),sQuery(id+"F0.wireOp",EDGE,"E40.0.4.0"),sQuery(id+"F0.wireOp",EDGE,"E41"),sQuery(id+"F0.wireOp",EDGE,"E42.0.1.0"),sQuery(id+"F0.wireOp",EDGE,"E42.1.0.0"),sQuery(id+"F0.wireOp",EDGE,"E42.1.1.0"),sQuery(id+"F0.wireOp",EDGE,"E42.2.0.0"),sQuery(id+"F0.wireOp",EDGE,"E42.2.1.0"),sQuery(id+"F0.wireOp",EDGE,"E42.3.0.0"),sQuery(id+"F0.wireOp",EDGE,"E42.3.1.0"),sQuery(id+"F0.wireOp",EDGE,"E45"),sQuery(id+"F0.wireOp",EDGE,"E46"),sQuery(id+"F0.wireOp",EDGE,"E47"),sQuery(id+"F0.wireOp",EDGE,"E48")])],"isStart":true});
            extrude(context, id + "F13", {"entities" : qUnion([Q0, Q1, Q2]), "operationType" : NewBodyOperationType.ADD, "depth" : 0.76 * mm, "hasSecondDirection" : true, "secondDirectionBound" : SecondDirectionBoundingType.UP_TO_SURFACE, "secondDirectionOppositeDirection" : true, "secondDirectionBoundEntityFace" : qUnion([Q3]), "secondDirectionDepth" : 25.4 * mm});
        }
        {
            var Q0;
            Q0=makeQuery(id+"F0.imprint","IMPRINT",FACE,{"disambiguationData":[TD([[makeQuery(id+"F0.imprint","IMPRINT",EDGE,{"derivedFrom":sQuery(id+"F0.wireOp",EDGE,"E42.1.0.0")}),1.0]])]});
            var Q1;
            Q1=makeQuery(id+"F0.imprint","IMPRINT",FACE,{"disambiguationData":[TD([[makeQuery(id+"F0.imprint","IMPRINT",EDGE,{"derivedFrom":sQuery(id+"F0.wireOp",EDGE,"E42.1.1.0")}),1.0]])]});
            extrude(context, id + "F14", {"entities" : qUnion([Q0, Q1]), "operationType" : NewBodyOperationType.ADD, "oppositeDirection" : true, "depth" : 1.59 * mm});
        }
        {
            var Q0;
            Q0=makeQuery(id+"F1.opExtrude","CAP_FACE",FACE,{"disambiguationData":[OSD([sQuery(id+"F0.wireOp",EDGE,"E31.bottom"),sQuery(id+"F0.wireOp",EDGE,"E31.top"),sQuery(id+"F0.wireOp",EDGE,"E31.left"),sQuery(id+"F0.wireOp",EDGE,"E31.right"),sQuery(id+"F0.wireOp",EDGE,"E32.filletArc"),sQuery(id+"F0.wireOp",EDGE,"E33.filletArc"),sQuery(id+"F0.wireOp",EDGE,"E34.filletArc"),sQuery(id+"F0.wireOp",EDGE,"E35.filletArc"),sQuery(id+"F0.wireOp",EDGE,"E36"),sQuery(id+"F0.wireOp",EDGE,"E37"),sQuery(id+"F0.wireOp",EDGE,"E38"),sQuery(id+"F0.wireOp",EDGE,"E39.0.1.0"),sQuery(id+"F0.wireOp",EDGE,"E39.0.2.0"),sQuery(id+"F0.wireOp",EDGE,"E39.0.3.0"),sQuery(id+"F0.wireOp",EDGE,"E39.0.4.0"),sQuery(id+"F0.wireOp",EDGE,"E40.0.1.0"),sQuery(id+"F0.wireOp",EDGE,"E40.0.2.0"),sQuery(id+"F0.wireOp",EDGE,"E40.0.3.0"),sQuery(id+"F0.wireOp",EDGE,"E40.0.4.0"),sQuery(id+"F0.wireOp",EDGE,"E41"),sQuery(id+"F0.wireOp",EDGE,"E42.0.1.0"),sQuery(id+"F0.wireOp",EDGE,"E42.1.0.0"),sQuery(id+"F0.wireOp",EDGE,"E42.1.1.0"),sQuery(id+"F0.wireOp",EDGE,"E42.2.0.0"),sQuery(id+"F0.wireOp",EDGE,"E42.2.1.0"),sQuery(id+"F0.wireOp",EDGE,"E42.3.0.0"),sQuery(id+"F0.wireOp",EDGE,"E42.3.1.0"),sQuery(id+"F0.wireOp",EDGE,"E45"),sQuery(id+"F0.wireOp",EDGE,"E46"),sQuery(id+"F0.wireOp",EDGE,"E47"),sQuery(id+"F0.wireOp",EDGE,"E48")])],"isStart":false});
            var sketch = newSketch(context, id + "F15", { "sketchPlane" : qUnion([Q0])});
            skLineSegment(sketch, "E155.bottom", {"start": v(23.62, -20.83) * mm, "end": v(16.64, -20.83) * mm});
            skLineSegment(sketch, "E155.top", {"start": v(23.62, -27.69) * mm, "end": v(16.64, -27.69) * mm});
            skLineSegment(sketch, "E155.left", {"start": v(23.62, -20.83) * mm, "end": v(23.62, -27.69) * mm});
            skLineSegment(sketch, "E155.right", {"start": v(16.64, -20.83) * mm, "end": v(16.64, -27.69) * mm});
            skLineSegment(sketch, "E156", {"start": v(20.07, -22.48) * mm, "end": v(20.07, -26.03) * mm, "construction": true});
            skLineSegment(sketch, "E157", {"start": v(20.07, -24.26) * mm, "end": v(23.62, -24.26) * mm, "construction": true});
            skLineSegment(sketch, "E158.bottom", {"start": v(23.62, -19.81) * mm, "end": v(16.64, -19.81) * mm});
            skLineSegment(sketch, "E158.top", {"start": v(23.62, -12.95) * mm, "end": v(16.64, -12.95) * mm});
            skLineSegment(sketch, "E158.left", {"start": v(23.62, -19.81) * mm, "end": v(23.62, -12.95) * mm});
            skLineSegment(sketch, "E158.right", {"start": v(16.64, -19.81) * mm, "end": v(16.64, -12.95) * mm});
            skLineSegment(sketch, "E159", {"start": v(20.07, -14.6) * mm, "end": v(20.07, -18.16) * mm, "construction": true});
            skLineSegment(sketch, "E160", {"start": v(23.62, -16.38) * mm, "end": v(20.07, -16.38) * mm, "construction": true});
            skSolve(sketch);
        }
        {
            var Q0;
            Q0=makeQuery(id+"F15.imprint","IMPRINT",FACE,{"disambiguationData":[TD([[makeQuery(id+"F15.imprint","IMPRINT",EDGE,{"derivedFrom":sQuery(id+"F15.wireOp",EDGE,"E158.bottom")}),-1.0]])]});
            var Q1;
            Q1=makeQuery(id+"F15.imprint","IMPRINT",FACE,{"disambiguationData":[TD([[makeQuery(id+"F15.imprint","IMPRINT",EDGE,{"derivedFrom":sQuery(id+"F15.wireOp",EDGE,"E155.bottom")}),1.0]])]});
            var Q2;
            Q2=makeQuery(id+"F15.imprint","IMPRINT",FACE,{"disambiguationData":[TD([[makeQuery(id+"F15.imprint","IMPRINT",EDGE,{"derivedFrom":makeQuery(id+"F1.opExtrude","CAP_EDGE",EDGE,{"disambiguationData":[OSD([sQuery(id+"F0.wireOp",EDGE,"E45")])],"isStart":false})}),1.0]])]});
            var Q3;
            Q3=makeQuery(id+"F15.imprint","IMPRINT",FACE,{"disambiguationData":[TD([[makeQuery(id+"F15.imprint","IMPRINT",EDGE,{"derivedFrom":makeQuery(id+"F1.opExtrude","CAP_EDGE",EDGE,{"disambiguationData":[OSD([sQuery(id+"F0.wireOp",EDGE,"E46")])],"isStart":false})}),1.0]])]});
            var Q4;
            Q4=makeQuery(id+"F15.imprint","IMPRINT",FACE,{"disambiguationData":[TD([[makeQuery(id+"F15.imprint","IMPRINT",EDGE,{"derivedFrom":makeQuery(id+"F1.opExtrude","CAP_EDGE",EDGE,{"disambiguationData":[OSD([sQuery(id+"F0.wireOp",EDGE,"E48")])],"isStart":false})}),1.0]])]});
            var Q5;
            Q5=makeQuery(id+"F15.imprint","IMPRINT",FACE,{"disambiguationData":[TD([[makeQuery(id+"F15.imprint","IMPRINT",EDGE,{"derivedFrom":makeQuery(id+"F1.opExtrude","CAP_EDGE",EDGE,{"disambiguationData":[OSD([sQuery(id+"F0.wireOp",EDGE,"E47")])],"isStart":false})}),1.0]])]});
            extrude(context, id + "F16", {"entities" : qUnion([Q0, Q1, Q2, Q3, Q4, Q5]), "operationType" : NewBodyOperationType.ADD, "depth" : 8.38 * mm});
        }
        {
            var Q0;
            Q0=makeQuery(id+"F16.opExtrude","CAP_EDGE",EDGE,{"disambiguationData":[OSD([sQuery(id+"F15.wireOp",EDGE,"E155.left")])],"isStart":false});
            chamfer(context, id + "F17", {"entities" : qUnion([Q0]), "chamferType" : ChamferType.TWO_OFFSETS, "width1" : 3.17 * mm, "oppositeDirection" : false, "width2" : 1.59 * mm, "tangentPropagation" : true});
        }
        {
            var Q0;
            Q0=makeQuery(id+"F16.opExtrude","CAP_EDGE",EDGE,{"disambiguationData":[OSD([sQuery(id+"F15.wireOp",EDGE,"E158.left")])],"isStart":false});
            chamfer(context, id + "F18", {"entities" : qUnion([Q0]), "chamferType" : ChamferType.TWO_OFFSETS, "width1" : 3.17 * mm, "oppositeDirection" : true, "width2" : 1.59 * mm, "tangentPropagation" : true});
        }
        {
            var Q0;
            Q0=makeQuery(id+"F16.opExtrude","SWEPT_FACE",FACE,{"disambiguationData":[OSD([sQuery(id+"F15.wireOp",EDGE,"E155.left")])]});
            var sketch = newSketch(context, id + "F19", { "sketchPlane" : qUnion([Q0])});
            skCircle(sketch, "E161", {"center": v(-26.03, 3.87) * mm, "radius": 0.5 * mm});
            skCircle(sketch, "E162", {"center": v(-22.48, 3.87) * mm, "radius": 0.5 * mm});
            skLineSegment(sketch, "E163.0", {"start": v(-26.54, 0) * mm, "end": v(-25.53, 0) * mm});
            skLineSegment(sketch, "E164.0", {"start": v(-22.99, 0) * mm, "end": v(-21.97, 0) * mm});
            skPoint(sketch, "E165", {"position": v(-26.03, 0) * mm});
            skPoint(sketch, "E166", {"position": v(-22.48, 0) * mm});
            skSolve(sketch);
        }
        {
            var Q0;
            Q0=makeQuery(id+"F19.imprint","IMPRINT",FACE,{"disambiguationData":[TD([[makeQuery(id+"F19.imprint","IMPRINT",EDGE,{"derivedFrom":sQuery(id+"F19.wireOp",EDGE,"E161")}),1.0]])]});
            var Q1;
            Q1=makeQuery(id+"F19.imprint","IMPRINT",FACE,{"disambiguationData":[TD([[makeQuery(id+"F19.imprint","IMPRINT",EDGE,{"derivedFrom":sQuery(id+"F19.wireOp",EDGE,"E162")}),1.0]])]});
            extrude(context, id + "F20", {"entities" : qUnion([Q0, Q1]), "operationType" : NewBodyOperationType.ADD, "depth" : 3.17 * mm});
        }
        {
            var Q0;
            Q0=makeQuery(id+"F0.imprint","IMPRINT",FACE,{"disambiguationData":[TD([[makeQuery(id+"F0.imprint","IMPRINT",EDGE,{"derivedFrom":sQuery(id+"F0.wireOp",EDGE,"E45")}),1.0]])]});
            var Q1;
            Q1=makeQuery(id+"F0.imprint","IMPRINT",FACE,{"disambiguationData":[TD([[makeQuery(id+"F0.imprint","IMPRINT",EDGE,{"derivedFrom":sQuery(id+"F0.wireOp",EDGE,"E46")}),1.0]])]});
            extrude(context, id + "F21", {"entities" : qUnion([Q0, Q1]), "operationType" : NewBodyOperationType.ADD, "oppositeDirection" : true, "depth" : 1.59 * mm, "hasSecondDirection" : true, "secondDirectionOppositeDirection" : false, "secondDirectionDepth" : 6.35 * mm});
        }
        {
            var Q0;
            Q0=makeQuery(id+"F14.opExtrude","SWEPT_FACE",FACE,{"disambiguationData":[OSD([sQuery(id+"F0.wireOp",EDGE,"E42.1.0.0")])]});
            var Q1;
            Q1=makeQuery(id+"F14.opExtrude","SWEPT_FACE",FACE,{"disambiguationData":[OSD([sQuery(id+"F0.wireOp",EDGE,"E42.1.1.0")])]});
            var Q2;
            Q2=makeQuery(id+"F21.opExtrude","SWEPT_FACE",FACE,{"disambiguationData":[OSD([sQuery(id+"F0.wireOp",EDGE,"E46")])]});
            var Q3;
            Q3=makeQuery(id+"F21.opExtrude","SWEPT_FACE",FACE,{"disambiguationData":[OSD([sQuery(id+"F0.wireOp",EDGE,"E45")])]});
            var Q4;
            Q4=makeQuery(id+"F13.opExtrude","CAP_FACE",FACE,{"disambiguationData":[OSD([sQuery(id+"F0.wireOp",EDGE,"E42.1.0.0"),sQuery(id+"F0.wireOp",EDGE,"E42.1.1.0"),sQuery(id+"F12.wireOp",EDGE,"E153"),sQuery(id+"F12.wireOp",EDGE,"E154")])],"isStart":false});
            fillet(context, id + "F22", {"entities" : qUnion([Q0, Q1, Q2, Q3, Q4]), "radius" : 0.5 * mm, "tangentPropagation" : true, "allowEdgeOverflow" : false});
        }
        {
            var Q0;
            Q0=makeQuery(id+"F1.opExtrude","CAP_FACE",FACE,{"disambiguationData":[OSD([sQuery(id+"F0.wireOp",EDGE,"E31.bottom"),sQuery(id+"F0.wireOp",EDGE,"E31.top"),sQuery(id+"F0.wireOp",EDGE,"E31.left"),sQuery(id+"F0.wireOp",EDGE,"E31.right"),sQuery(id+"F0.wireOp",EDGE,"E32.filletArc"),sQuery(id+"F0.wireOp",EDGE,"E33.filletArc"),sQuery(id+"F0.wireOp",EDGE,"E34.filletArc"),sQuery(id+"F0.wireOp",EDGE,"E35.filletArc"),sQuery(id+"F0.wireOp",EDGE,"E36"),sQuery(id+"F0.wireOp",EDGE,"E37"),sQuery(id+"F0.wireOp",EDGE,"E38"),sQuery(id+"F0.wireOp",EDGE,"E39.0.1.0"),sQuery(id+"F0.wireOp",EDGE,"E39.0.2.0"),sQuery(id+"F0.wireOp",EDGE,"E39.0.3.0"),sQuery(id+"F0.wireOp",EDGE,"E39.0.4.0"),sQuery(id+"F0.wireOp",EDGE,"E40.0.1.0"),sQuery(id+"F0.wireOp",EDGE,"E40.0.2.0"),sQuery(id+"F0.wireOp",EDGE,"E40.0.3.0"),sQuery(id+"F0.wireOp",EDGE,"E40.0.4.0"),sQuery(id+"F0.wireOp",EDGE,"E41"),sQuery(id+"F0.wireOp",EDGE,"E42.0.1.0"),sQuery(id+"F0.wireOp",EDGE,"E42.1.0.0"),sQuery(id+"F0.wireOp",EDGE,"E42.1.1.0"),sQuery(id+"F0.wireOp",EDGE,"E42.2.0.0"),sQuery(id+"F0.wireOp",EDGE,"E42.2.1.0"),sQuery(id+"F0.wireOp",EDGE,"E42.3.0.0"),sQuery(id+"F0.wireOp",EDGE,"E42.3.1.0"),sQuery(id+"F0.wireOp",EDGE,"E45"),sQuery(id+"F0.wireOp",EDGE,"E46"),sQuery(id+"F0.wireOp",EDGE,"E47"),sQuery(id+"F0.wireOp",EDGE,"E48")])],"isStart":false});
            var sketch = newSketch(context, id + "F23", { "sketchPlane" : qUnion([Q0])});
            skLineSegment(sketch, "E167.bottom", {"start": v(6.38, -26.67) * mm, "end": v(8.4, -26.67) * mm});
            skLineSegment(sketch, "E167.top", {"start": v(6.38, -25.4) * mm, "end": v(8.4, -25.4) * mm});
            skLineSegment(sketch, "E167.left", {"start": v(6.38, -26.67) * mm, "end": v(6.38, -25.4) * mm});
            skLineSegment(sketch, "E167.right", {"start": v(8.4, -26.67) * mm, "end": v(8.4, -25.4) * mm});
            skLineSegment(sketch, "E168.bottom", {"start": v(14.88, -26.43) * mm, "end": v(12.85, -26.43) * mm});
            skLineSegment(sketch, "E168.top", {"start": v(14.88, -27.7) * mm, "end": v(12.85, -27.7) * mm});
            skLineSegment(sketch, "E168.left", {"start": v(14.88, -26.43) * mm, "end": v(14.88, -27.7) * mm});
            skLineSegment(sketch, "E168.right", {"start": v(12.85, -26.43) * mm, "end": v(12.85, -27.7) * mm});
            skLineSegment(sketch, "E169.bottom", {"start": v(14.88, -24.36) * mm, "end": v(12.85, -24.36) * mm});
            skLineSegment(sketch, "E169.top", {"start": v(14.88, -25.63) * mm, "end": v(12.85, -25.63) * mm});
            skLineSegment(sketch, "E169.left", {"start": v(14.88, -24.36) * mm, "end": v(14.88, -25.63) * mm});
            skLineSegment(sketch, "E169.right", {"start": v(12.85, -24.36) * mm, "end": v(12.85, -25.63) * mm});
            skLineSegment(sketch, "E170.bottom", {"start": v(9.2, -13.59) * mm, "end": v(7.92, -13.59) * mm});
            skLineSegment(sketch, "E170.top", {"start": v(9.2, -15.62) * mm, "end": v(7.92, -15.62) * mm});
            skLineSegment(sketch, "E170.left", {"start": v(9.2, -13.59) * mm, "end": v(9.2, -15.62) * mm});
            skLineSegment(sketch, "E170.right", {"start": v(7.92, -13.59) * mm, "end": v(7.92, -15.62) * mm});
            skLineSegment(sketch, "E171.bottom", {"start": v(11.43, -14.48) * mm, "end": v(12.7, -14.48) * mm});
            skLineSegment(sketch, "E171.top", {"start": v(11.43, -16.51) * mm, "end": v(12.7, -16.51) * mm});
            skLineSegment(sketch, "E171.left", {"start": v(11.43, -14.48) * mm, "end": v(11.43, -16.51) * mm});
            skLineSegment(sketch, "E171.right", {"start": v(12.7, -14.48) * mm, "end": v(12.7, -16.51) * mm});
            skLineSegment(sketch, "E172.bottom", {"start": v(13.61, -14.48) * mm, "end": v(14.88, -14.48) * mm});
            skLineSegment(sketch, "E172.top", {"start": v(13.61, -16.51) * mm, "end": v(14.88, -16.51) * mm});
            skLineSegment(sketch, "E172.left", {"start": v(13.61, -14.48) * mm, "end": v(13.61, -16.51) * mm});
            skLineSegment(sketch, "E172.right", {"start": v(14.88, -14.48) * mm, "end": v(14.88, -16.5) * mm});
            skLineSegment(sketch, "E173.bottom", {"start": v(11.84, -19.05) * mm, "end": v(14.76, -19.05) * mm});
            skLineSegment(sketch, "E173.top", {"start": v(11.84, -21.97) * mm, "end": v(14.76, -21.97) * mm});
            skLineSegment(sketch, "E173.left", {"start": v(11.84, -19.05) * mm, "end": v(11.84, -21.97) * mm});
            skLineSegment(sketch, "E173.right", {"start": v(14.76, -19.05) * mm, "end": v(14.76, -21.97) * mm});
            skLineSegment(sketch, "E174.0.1.0", {"start": v(6.38, -23.24) * mm, "end": v(8.4, -23.24) * mm});
            skLineSegment(sketch, "E174.0.1.1", {"start": v(8.4, -24.51) * mm, "end": v(8.4, -23.24) * mm});
            skLineSegment(sketch, "E174.0.1.2", {"start": v(6.38, -24.51) * mm, "end": v(8.4, -24.51) * mm});
            skLineSegment(sketch, "E174.0.1.3", {"start": v(6.38, -24.51) * mm, "end": v(6.38, -23.24) * mm});
            skLineSegment(sketch, "E174.0.2.0", {"start": v(6.38, -21.08) * mm, "end": v(8.4, -21.08) * mm});
            skLineSegment(sketch, "E174.0.2.1", {"start": v(8.4, -22.35) * mm, "end": v(8.4, -21.08) * mm});
            skLineSegment(sketch, "E174.0.2.2", {"start": v(6.38, -22.35) * mm, "end": v(8.4, -22.35) * mm});
            skLineSegment(sketch, "E174.0.2.3", {"start": v(6.38, -22.35) * mm, "end": v(6.38, -21.08) * mm});
            skLineSegment(sketch, "E174.0.3.0", {"start": v(6.38, -18.92) * mm, "end": v(8.4, -18.92) * mm});
            skLineSegment(sketch, "E174.0.3.1", {"start": v(8.4, -20.2) * mm, "end": v(8.4, -18.92) * mm});
            skLineSegment(sketch, "E174.0.3.2", {"start": v(6.38, -20.2) * mm, "end": v(8.4, -20.2) * mm});
            skLineSegment(sketch, "E174.0.3.3", {"start": v(6.38, -20.2) * mm, "end": v(6.38, -18.92) * mm});
            skLineSegment(sketch, "E174.0.4.0", {"start": v(6.38, -16.76) * mm, "end": v(8.4, -16.76) * mm});
            skLineSegment(sketch, "E174.0.4.1", {"start": v(8.4, -18.03) * mm, "end": v(8.4, -16.76) * mm});
            skLineSegment(sketch, "E174.0.4.2", {"start": v(6.38, -18.03) * mm, "end": v(8.4, -18.03) * mm});
            skLineSegment(sketch, "E174.0.4.3", {"start": v(6.38, -18.03) * mm, "end": v(6.38, -16.76) * mm});
            skLineSegment(sketch, "E174.direction1", {"start": v(6.38, -25.4) * mm, "end": v(8.4, -25.4) * mm, "construction": true});
            skLineSegment(sketch, "E174.direction2", {"start": v(6.38, -25.4) * mm, "end": v(6.38, -23.24) * mm, "construction": true});
            skLineSegment(sketch, "E175.bottom", {"start": v(35.56, 10.16) * mm, "end": v(43.18, 10.16) * mm});
            skLineSegment(sketch, "E175.top", {"start": v(35.56, 4.67) * mm, "end": v(43.18, 4.67) * mm});
            skLineSegment(sketch, "E175.left", {"start": v(35.56, 10.16) * mm, "end": v(35.56, 4.67) * mm});
            skLineSegment(sketch, "E175.right", {"start": v(43.18, 10.16) * mm, "end": v(43.18, 4.67) * mm});
            skLineSegment(sketch, "E176.0", {"start": v(31.75, 10.16) * mm, "end": v(47, 10.16) * mm, "construction": true});
            skPoint(sketch, "E177", {"position": v(39.37, 10.16) * mm});
            skLineSegment(sketch, "E178.bottom", {"start": v(-25.15, 13.08) * mm, "end": v(-23.11, 13.08) * mm});
            skLineSegment(sketch, "E178.top", {"start": v(-25.15, 11.81) * mm, "end": v(-23.11, 11.81) * mm});
            skLineSegment(sketch, "E178.left", {"start": v(-25.15, 13.08) * mm, "end": v(-25.15, 11.81) * mm});
            skLineSegment(sketch, "E178.right", {"start": v(-23.11, 13.08) * mm, "end": v(-23.11, 11.81) * mm});
            skLineSegment(sketch, "E179.bottom", {"start": v(-25.55, 9.9) * mm, "end": v(-22.6, 9.9) * mm});
            skLineSegment(sketch, "E179.top", {"start": v(-25.55, 8.32) * mm, "end": v(-22.6, 8.32) * mm});
            skLineSegment(sketch, "E179.left", {"start": v(-25.55, 9.9) * mm, "end": v(-25.55, 8.32) * mm});
            skLineSegment(sketch, "E179.right", {"start": v(-22.6, 9.9) * mm, "end": v(-22.6, 8.32) * mm});
            skLineSegment(sketch, "E180.bottom", {"start": v(-25.15, 6.35) * mm, "end": v(-23.11, 6.35) * mm});
            skLineSegment(sketch, "E180.top", {"start": v(-25.15, 5.08) * mm, "end": v(-23.11, 5.08) * mm});
            skLineSegment(sketch, "E180.left", {"start": v(-25.15, 6.35) * mm, "end": v(-25.15, 5.08) * mm});
            skLineSegment(sketch, "E180.right", {"start": v(-23.11, 6.35) * mm, "end": v(-23.11, 5.08) * mm});
            skLineSegment(sketch, "E181.bottom", {"start": v(-21.65, 8.89) * mm, "end": v(-18.73, 8.9) * mm});
            skLineSegment(sketch, "E181.top", {"start": v(-21.65, 7.62) * mm, "end": v(-18.73, 7.62) * mm});
            skLineSegment(sketch, "E181.left", {"start": v(-21.65, 8.89) * mm, "end": v(-21.65, 7.62) * mm});
            skLineSegment(sketch, "E181.right", {"start": v(-18.73, 8.9) * mm, "end": v(-18.73, 7.62) * mm});
            skLineSegment(sketch, "E182.bottom", {"start": v(-20.83, 10.8) * mm, "end": v(-19.56, 10.8) * mm});
            skLineSegment(sketch, "E182.top", {"start": v(-20.83, 12.83) * mm, "end": v(-19.56, 12.83) * mm});
            skLineSegment(sketch, "E182.left", {"start": v(-20.83, 10.8) * mm, "end": v(-20.83, 12.83) * mm});
            skLineSegment(sketch, "E182.right", {"start": v(-19.56, 10.8) * mm, "end": v(-19.56, 12.83) * mm});
            skLineSegment(sketch, "E183.bottom", {"start": v(-14.78, 11.73) * mm, "end": v(-17.78, 11.73) * mm});
            skLineSegment(sketch, "E183.top", {"start": v(-14.78, 8.74) * mm, "end": v(-17.78, 8.74) * mm});
            skLineSegment(sketch, "E183.left", {"start": v(-14.78, 11.73) * mm, "end": v(-14.78, 8.74) * mm});
            skLineSegment(sketch, "E183.right", {"start": v(-17.78, 11.73) * mm, "end": v(-17.78, 8.74) * mm});
            skLineSegment(sketch, "E184.bottom", {"start": v(-14.6, 13.84) * mm, "end": v(-12.57, 13.84) * mm});
            skLineSegment(sketch, "E184.top", {"start": v(-14.6, 12.57) * mm, "end": v(-12.57, 12.57) * mm});
            skLineSegment(sketch, "E184.left", {"start": v(-14.6, 13.84) * mm, "end": v(-14.6, 12.57) * mm});
            skLineSegment(sketch, "E184.right", {"start": v(-12.57, 13.84) * mm, "end": v(-12.57, 12.57) * mm});
            skLineSegment(sketch, "E185.bottom", {"start": v(-18.67, 6.22) * mm, "end": v(-16.64, 6.22) * mm});
            skLineSegment(sketch, "E185.top", {"start": v(-18.67, 4.95) * mm, "end": v(-16.64, 4.95) * mm});
            skLineSegment(sketch, "E185.left", {"start": v(-18.67, 6.22) * mm, "end": v(-18.67, 4.95) * mm});
            skLineSegment(sketch, "E185.right", {"start": v(-16.64, 6.22) * mm, "end": v(-16.64, 4.95) * mm});
            skLineSegment(sketch, "E186.bottom", {"start": v(-15.09, 6.22) * mm, "end": v(-13.06, 6.22) * mm});
            skLineSegment(sketch, "E186.top", {"start": v(-15.09, 4.95) * mm, "end": v(-13.06, 4.95) * mm});
            skLineSegment(sketch, "E186.left", {"start": v(-15.09, 6.22) * mm, "end": v(-15.09, 4.95) * mm});
            skLineSegment(sketch, "E186.right", {"start": v(-13.06, 6.22) * mm, "end": v(-13.06, 4.95) * mm});
            skLineSegment(sketch, "E187.bottom", {"start": v(-12.7, 8.15) * mm, "end": v(-10.67, 8.15) * mm});
            skLineSegment(sketch, "E187.top", {"start": v(-12.7, 6.88) * mm, "end": v(-10.67, 6.88) * mm});
            skLineSegment(sketch, "E187.left", {"start": v(-12.7, 8.15) * mm, "end": v(-12.7, 6.88) * mm});
            skLineSegment(sketch, "E187.right", {"start": v(-10.67, 8.15) * mm, "end": v(-10.67, 6.88) * mm});
            skLineSegment(sketch, "E188.bottom", {"start": v(-9.27, 6.22) * mm, "end": v(-7.24, 6.22) * mm});
            skLineSegment(sketch, "E188.top", {"start": v(-9.27, 4.95) * mm, "end": v(-7.24, 4.95) * mm});
            skLineSegment(sketch, "E188.left", {"start": v(-9.27, 6.22) * mm, "end": v(-9.27, 4.95) * mm});
            skLineSegment(sketch, "E188.right", {"start": v(-7.24, 6.22) * mm, "end": v(-7.24, 4.95) * mm});
            skLineSegment(sketch, "E189.bottom", {"start": v(-12.32, 10.92) * mm, "end": v(-9.4, 10.92) * mm});
            skLineSegment(sketch, "E189.top", {"start": v(-12.32, 9.65) * mm, "end": v(-9.4, 9.65) * mm});
            skLineSegment(sketch, "E189.left", {"start": v(-12.32, 10.92) * mm, "end": v(-12.32, 9.65) * mm});
            skLineSegment(sketch, "E189.right", {"start": v(-9.4, 10.92) * mm, "end": v(-9.4, 9.65) * mm});
            skLineSegment(sketch, "E190.bottom", {"start": v(-7.11, 10.03) * mm, "end": v(-8.38, 10.03) * mm});
            skLineSegment(sketch, "E190.top", {"start": v(-7.11, 8) * mm, "end": v(-8.38, 8) * mm});
            skLineSegment(sketch, "E190.left", {"start": v(-7.11, 10.03) * mm, "end": v(-7.11, 8) * mm});
            skLineSegment(sketch, "E190.right", {"start": v(-8.38, 10.03) * mm, "end": v(-8.38, 8) * mm});
            skLineSegment(sketch, "E191.bottom", {"start": v(-9.65, 12.95) * mm, "end": v(-7.62, 12.95) * mm});
            skLineSegment(sketch, "E191.top", {"start": v(-9.65, 11.68) * mm, "end": v(-7.62, 11.68) * mm});
            skLineSegment(sketch, "E191.left", {"start": v(-9.65, 12.95) * mm, "end": v(-9.65, 11.68) * mm});
            skLineSegment(sketch, "E191.right", {"start": v(-7.62, 12.95) * mm, "end": v(-7.62, 11.68) * mm});
            skLineSegment(sketch, "E192.bottom", {"start": v(-22.99, -18.39) * mm, "end": v(-24.26, -18.39) * mm});
            skLineSegment(sketch, "E192.top", {"start": v(-22.99, -21.31) * mm, "end": v(-24.26, -21.31) * mm});
            skLineSegment(sketch, "E192.left", {"start": v(-22.99, -18.39) * mm, "end": v(-22.99, -21.31) * mm});
            skLineSegment(sketch, "E192.right", {"start": v(-24.26, -18.39) * mm, "end": v(-24.26, -21.31) * mm});
            skLineSegment(sketch, "E193.bottom", {"start": v(-20.83, -20.45) * mm, "end": v(-17.9, -20.45) * mm});
            skLineSegment(sketch, "E193.top", {"start": v(-20.83, -21.72) * mm, "end": v(-17.9, -21.72) * mm});
            skLineSegment(sketch, "E193.left", {"start": v(-20.83, -20.45) * mm, "end": v(-20.83, -21.72) * mm});
            skLineSegment(sketch, "E193.right", {"start": v(-17.9, -20.45) * mm, "end": v(-17.9, -21.72) * mm});
            skLineSegment(sketch, "E194.bottom", {"start": v(-20.45, -15.11) * mm, "end": v(-18.41, -15.11) * mm});
            skLineSegment(sketch, "E194.top", {"start": v(-20.45, -17.9) * mm, "end": v(-18.41, -17.9) * mm});
            skLineSegment(sketch, "E194.left", {"start": v(-20.45, -15.11) * mm, "end": v(-20.45, -17.9) * mm});
            skLineSegment(sketch, "E194.right", {"start": v(-18.41, -15.11) * mm, "end": v(-18.41, -17.9) * mm});
            skLineSegment(sketch, "E195.bottom", {"start": v(-21.6, -14.6) * mm, "end": v(-22.86, -14.6) * mm});
            skLineSegment(sketch, "E195.top", {"start": v(-21.6, -16.64) * mm, "end": v(-22.86, -16.64) * mm});
            skLineSegment(sketch, "E195.left", {"start": v(-21.6, -14.6) * mm, "end": v(-21.6, -16.64) * mm});
            skLineSegment(sketch, "E195.right", {"start": v(-22.86, -14.6) * mm, "end": v(-22.86, -16.64) * mm});
            skLineSegment(sketch, "E196.bottom", {"start": v(-24.13, -14.6) * mm, "end": v(-25.4, -14.6) * mm});
            skLineSegment(sketch, "E196.top", {"start": v(-24.13, -16.64) * mm, "end": v(-25.4, -16.64) * mm});
            skLineSegment(sketch, "E196.left", {"start": v(-24.13, -14.6) * mm, "end": v(-24.13, -16.64) * mm});
            skLineSegment(sketch, "E196.right", {"start": v(-25.4, -14.6) * mm, "end": v(-25.4, -16.64) * mm});
            skLineSegment(sketch, "E197.bottom", {"start": v(-20.32, -12.07) * mm, "end": v(-18.29, -12.07) * mm});
            skLineSegment(sketch, "E197.top", {"start": v(-20.32, -13.34) * mm, "end": v(-18.29, -13.34) * mm});
            skLineSegment(sketch, "E197.left", {"start": v(-20.32, -12.07) * mm, "end": v(-20.32, -13.34) * mm});
            skLineSegment(sketch, "E197.right", {"start": v(-18.29, -12.07) * mm, "end": v(-18.29, -13.34) * mm});
            skLineSegment(sketch, "E198.bottom", {"start": v(-16.38, -12.07) * mm, "end": v(-13.46, -12.07) * mm});
            skLineSegment(sketch, "E198.top", {"start": v(-16.38, -13.34) * mm, "end": v(-13.46, -13.34) * mm});
            skLineSegment(sketch, "E198.left", {"start": v(-16.38, -12.06) * mm, "end": v(-16.38, -13.34) * mm});
            skLineSegment(sketch, "E198.right", {"start": v(-13.46, -12.06) * mm, "end": v(-13.46, -13.34) * mm});
            skLineSegment(sketch, "E199.bottom", {"start": v(-11.94, -15.11) * mm, "end": v(-13.2, -15.11) * mm});
            skLineSegment(sketch, "E199.top", {"start": v(-11.94, -17.14) * mm, "end": v(-13.2, -17.14) * mm});
            skLineSegment(sketch, "E199.left", {"start": v(-11.94, -15.11) * mm, "end": v(-11.94, -17.14) * mm});
            skLineSegment(sketch, "E199.right", {"start": v(-13.2, -15.11) * mm, "end": v(-13.2, -17.14) * mm});
            skLineSegment(sketch, "E200.bottom", {"start": v(-10.41, -14.86) * mm, "end": v(-8.38, -14.86) * mm});
            skLineSegment(sketch, "E200.top", {"start": v(-10.41, -16.13) * mm, "end": v(-8.38, -16.13) * mm});
            skLineSegment(sketch, "E200.left", {"start": v(-10.41, -14.86) * mm, "end": v(-10.41, -16.13) * mm});
            skLineSegment(sketch, "E200.right", {"start": v(-8.38, -14.86) * mm, "end": v(-8.38, -16.13) * mm});
            skLineSegment(sketch, "E201.bottom", {"start": v(-8.45, -17.02) * mm, "end": v(-10.03, -17.02) * mm});
            skLineSegment(sketch, "E201.top", {"start": v(-8.45, -19.81) * mm, "end": v(-10.03, -19.81) * mm});
            skLineSegment(sketch, "E201.left", {"start": v(-8.45, -17.02) * mm, "end": v(-8.45, -19.81) * mm});
            skLineSegment(sketch, "E201.right", {"start": v(-10.03, -17.02) * mm, "end": v(-10.03, -19.81) * mm});
            skLineSegment(sketch, "E202.bottom", {"start": v(-7.92, -20.96) * mm, "end": v(-9.96, -20.96) * mm});
            skLineSegment(sketch, "E202.top", {"start": v(-7.92, -22.23) * mm, "end": v(-9.96, -22.23) * mm});
            skLineSegment(sketch, "E202.left", {"start": v(-7.92, -20.96) * mm, "end": v(-7.92, -22.23) * mm});
            skLineSegment(sketch, "E202.right", {"start": v(-9.96, -20.96) * mm, "end": v(-9.96, -22.23) * mm});
            skLineSegment(sketch, "E203.bottom", {"start": v(-12.2, -20.96) * mm, "end": v(-14.22, -20.96) * mm});
            skLineSegment(sketch, "E203.top", {"start": v(-12.2, -22.23) * mm, "end": v(-14.22, -22.23) * mm});
            skLineSegment(sketch, "E203.left", {"start": v(-12.2, -20.96) * mm, "end": v(-12.2, -22.23) * mm});
            skLineSegment(sketch, "E203.right", {"start": v(-14.22, -20.96) * mm, "end": v(-14.22, -22.23) * mm});
            skLineSegment(sketch, "E204.bottom", {"start": v(-12.45, -18.67) * mm, "end": v(-14.48, -18.67) * mm});
            skLineSegment(sketch, "E204.top", {"start": v(-12.45, -19.94) * mm, "end": v(-14.48, -19.94) * mm});
            skLineSegment(sketch, "E204.left", {"start": v(-12.45, -18.67) * mm, "end": v(-12.45, -19.94) * mm});
            skLineSegment(sketch, "E204.right", {"start": v(-14.48, -18.67) * mm, "end": v(-14.48, -19.94) * mm});
            skLineSegment(sketch, "E205.bottom", {"start": v(-15.75, -19.81) * mm, "end": v(-17.02, -19.81) * mm});
            skLineSegment(sketch, "E205.top", {"start": v(-15.75, -21.84) * mm, "end": v(-17.02, -21.84) * mm});
            skLineSegment(sketch, "E205.left", {"start": v(-15.75, -19.81) * mm, "end": v(-15.75, -21.84) * mm});
            skLineSegment(sketch, "E205.right", {"start": v(-17.02, -19.81) * mm, "end": v(-17.02, -21.84) * mm});
            skLineSegment(sketch, "E206.bottom", {"start": v(-15.24, -15.5) * mm, "end": v(-17.27, -15.5) * mm});
            skLineSegment(sketch, "E206.top", {"start": v(-15.24, -17.78) * mm, "end": v(-17.27, -17.78) * mm});
            skLineSegment(sketch, "E206.left", {"start": v(-15.24, -15.5) * mm, "end": v(-15.24, -17.78) * mm});
            skLineSegment(sketch, "E206.right", {"start": v(-17.27, -15.5) * mm, "end": v(-17.27, -17.78) * mm});
            skLineSegment(sketch, "E207.bottom", {"start": v(37.72, -17.02) * mm, "end": v(39.75, -17.02) * mm});
            skLineSegment(sketch, "E207.top", {"start": v(37.72, -14.99) * mm, "end": v(39.75, -14.99) * mm});
            skLineSegment(sketch, "E207.left", {"start": v(37.72, -17.02) * mm, "end": v(37.72, -14.99) * mm});
            skLineSegment(sketch, "E207.right", {"start": v(39.75, -17.02) * mm, "end": v(39.75, -14.99) * mm});
            skLineSegment(sketch, "E208.bottom", {"start": v(36.83, -12.06) * mm, "end": v(35.56, -12.06) * mm});
            skLineSegment(sketch, "E208.top", {"start": v(36.83, -14.1) * mm, "end": v(35.56, -14.1) * mm});
            skLineSegment(sketch, "E208.left", {"start": v(36.83, -12.07) * mm, "end": v(36.83, -14.1) * mm});
            skLineSegment(sketch, "E208.right", {"start": v(35.56, -12.06) * mm, "end": v(35.56, -14.1) * mm});
            skLineSegment(sketch, "E209.bottom", {"start": v(37.6, -12.07) * mm, "end": v(40.51, -12.07) * mm});
            skLineSegment(sketch, "E209.top", {"start": v(37.6, -13.34) * mm, "end": v(40.51, -13.34) * mm});
            skLineSegment(sketch, "E209.left", {"start": v(37.6, -12.07) * mm, "end": v(37.6, -13.34) * mm});
            skLineSegment(sketch, "E209.right", {"start": v(40.51, -12.07) * mm, "end": v(40.51, -13.34) * mm});
            skLineSegment(sketch, "E210.bottom", {"start": v(42.98, -11.68) * mm, "end": v(41.7, -11.68) * mm});
            skLineSegment(sketch, "E210.top", {"start": v(42.98, -13.72) * mm, "end": v(41.7, -13.72) * mm});
            skLineSegment(sketch, "E210.left", {"start": v(42.98, -11.68) * mm, "end": v(42.98, -13.72) * mm});
            skLineSegment(sketch, "E210.right", {"start": v(41.7, -11.68) * mm, "end": v(41.7, -13.72) * mm});
            skLineSegment(sketch, "E211.bottom", {"start": v(42.98, -15.24) * mm, "end": v(41.7, -15.24) * mm});
            skLineSegment(sketch, "E211.top", {"start": v(42.98, -17.27) * mm, "end": v(41.7, -17.27) * mm});
            skLineSegment(sketch, "E211.left", {"start": v(42.98, -15.24) * mm, "end": v(42.98, -17.27) * mm});
            skLineSegment(sketch, "E211.right", {"start": v(41.7, -15.24) * mm, "end": v(41.7, -17.27) * mm});
            skLineSegment(sketch, "E212.bottom", {"start": v(46.35, -12.32) * mm, "end": v(44.32, -12.32) * mm});
            skLineSegment(sketch, "E212.top", {"start": v(46.35, -13.59) * mm, "end": v(44.32, -13.59) * mm});
            skLineSegment(sketch, "E212.left", {"start": v(46.35, -12.32) * mm, "end": v(46.35, -13.59) * mm});
            skLineSegment(sketch, "E212.right", {"start": v(44.32, -12.32) * mm, "end": v(44.32, -13.59) * mm});
            skLineSegment(sketch, "E213.bottom", {"start": v(46.23, -14.6) * mm, "end": v(44.96, -14.6) * mm});
            skLineSegment(sketch, "E213.top", {"start": v(46.23, -17.53) * mm, "end": v(44.96, -17.53) * mm});
            skLineSegment(sketch, "E213.left", {"start": v(46.23, -14.6) * mm, "end": v(46.23, -17.53) * mm});
            skLineSegment(sketch, "E213.right", {"start": v(44.96, -14.6) * mm, "end": v(44.96, -17.53) * mm});
            skLineSegment(sketch, "E214.bottom", {"start": v(33.53, -13.08) * mm, "end": v(32, -13.08) * mm});
            skLineSegment(sketch, "E214.top", {"start": v(33.53, -16) * mm, "end": v(32, -16) * mm});
            skLineSegment(sketch, "E214.left", {"start": v(33.53, -13.08) * mm, "end": v(33.53, -16) * mm});
            skLineSegment(sketch, "E214.right", {"start": v(32, -13.08) * mm, "end": v(32, -16) * mm});
            skLineSegment(sketch, "E215.bottom", {"start": v(33.53, -11.18) * mm, "end": v(31.5, -11.18) * mm});
            skLineSegment(sketch, "E215.top", {"start": v(33.53, -12.45) * mm, "end": v(31.5, -12.45) * mm});
            skLineSegment(sketch, "E215.left", {"start": v(33.53, -11.18) * mm, "end": v(33.53, -12.45) * mm});
            skLineSegment(sketch, "E215.right", {"start": v(31.5, -11.18) * mm, "end": v(31.5, -12.45) * mm});
            skLineSegment(sketch, "E216.bottom", {"start": v(34.04, -16.76) * mm, "end": v(32, -16.76) * mm});
            skLineSegment(sketch, "E216.top", {"start": v(34.04, -18.03) * mm, "end": v(32, -18.03) * mm});
            skLineSegment(sketch, "E216.left", {"start": v(34.04, -16.76) * mm, "end": v(34.04, -18.03) * mm});
            skLineSegment(sketch, "E216.right", {"start": v(32, -16.76) * mm, "end": v(32, -18.03) * mm});
            skLineSegment(sketch, "E217.bottom", {"start": v(29.97, 23.5) * mm, "end": v(31.24, 23.5) * mm});
            skLineSegment(sketch, "E217.top", {"start": v(29.97, 21.46) * mm, "end": v(31.24, 21.46) * mm});
            skLineSegment(sketch, "E217.left", {"start": v(29.97, 23.5) * mm, "end": v(29.97, 21.46) * mm});
            skLineSegment(sketch, "E217.right", {"start": v(31.24, 23.5) * mm, "end": v(31.24, 21.46) * mm});
            skLineSegment(sketch, "E218.bottom", {"start": v(32.13, 23.5) * mm, "end": v(33.4, 23.5) * mm});
            skLineSegment(sketch, "E218.top", {"start": v(32.13, 21.46) * mm, "end": v(33.4, 21.46) * mm});
            skLineSegment(sketch, "E218.left", {"start": v(32.13, 23.5) * mm, "end": v(32.13, 21.46) * mm});
            skLineSegment(sketch, "E218.right", {"start": v(33.4, 23.5) * mm, "end": v(33.4, 21.46) * mm});
            skLineSegment(sketch, "E219.bottom", {"start": v(34.3, 23.5) * mm, "end": v(35.56, 23.5) * mm});
            skLineSegment(sketch, "E219.top", {"start": v(34.3, 21.46) * mm, "end": v(35.56, 21.46) * mm});
            skLineSegment(sketch, "E219.left", {"start": v(34.3, 23.5) * mm, "end": v(34.3, 21.46) * mm});
            skLineSegment(sketch, "E219.right", {"start": v(35.56, 23.5) * mm, "end": v(35.56, 21.46) * mm});
            skLineSegment(sketch, "E220.bottom", {"start": v(37.97, 24.13) * mm, "end": v(41.02, 24.13) * mm});
            skLineSegment(sketch, "E220.top", {"start": v(37.97, 21.08) * mm, "end": v(41.02, 21.08) * mm});
            skLineSegment(sketch, "E220.left", {"start": v(37.97, 24.13) * mm, "end": v(37.97, 21.08) * mm});
            skLineSegment(sketch, "E220.right", {"start": v(41.02, 24.13) * mm, "end": v(41.02, 21.08) * mm});
            skLineSegment(sketch, "E221.bottom", {"start": v(43.18, 23.5) * mm, "end": v(44.45, 23.5) * mm});
            skLineSegment(sketch, "E221.top", {"start": v(43.18, 21.46) * mm, "end": v(44.45, 21.46) * mm});
            skLineSegment(sketch, "E221.left", {"start": v(43.18, 23.5) * mm, "end": v(43.18, 21.46) * mm});
            skLineSegment(sketch, "E221.right", {"start": v(44.45, 23.5) * mm, "end": v(44.45, 21.46) * mm});
            skLineSegment(sketch, "E222.bottom", {"start": v(45.34, 23.5) * mm, "end": v(46.6, 23.5) * mm});
            skLineSegment(sketch, "E222.top", {"start": v(45.34, 21.46) * mm, "end": v(46.6, 21.46) * mm});
            skLineSegment(sketch, "E222.left", {"start": v(45.34, 23.5) * mm, "end": v(45.34, 21.46) * mm});
            skLineSegment(sketch, "E222.right", {"start": v(46.6, 23.5) * mm, "end": v(46.6, 21.46) * mm});
            skLineSegment(sketch, "E223.bottom", {"start": v(47.5, 23.5) * mm, "end": v(48.77, 23.5) * mm});
            skLineSegment(sketch, "E223.top", {"start": v(47.5, 21.46) * mm, "end": v(48.77, 21.46) * mm});
            skLineSegment(sketch, "E223.left", {"start": v(47.5, 23.5) * mm, "end": v(47.5, 21.46) * mm});
            skLineSegment(sketch, "E223.right", {"start": v(48.77, 23.5) * mm, "end": v(48.77, 21.46) * mm});
            skSolve(sketch);
        }
        {
            var Q0;
            Q0=makeQuery(id+"F23.imprint","IMPRINT",FACE,{"disambiguationData":[TD([[makeQuery(id+"F23.imprint","IMPRINT",EDGE,{"derivedFrom":sQuery(id+"F23.wireOp",EDGE,"E170.bottom")}),1.0]])]});
            var Q1;
            Q1=makeQuery(id+"F23.imprint","IMPRINT",FACE,{"disambiguationData":[TD([[makeQuery(id+"F23.imprint","IMPRINT",EDGE,{"derivedFrom":sQuery(id+"F23.wireOp",EDGE,"E174.0.4.0")}),-1.0]])]});
            var Q2;
            Q2=makeQuery(id+"F23.imprint","IMPRINT",FACE,{"disambiguationData":[TD([[makeQuery(id+"F23.imprint","IMPRINT",EDGE,{"derivedFrom":sQuery(id+"F23.wireOp",EDGE,"E174.0.3.0")}),-1.0]])]});
            var Q3;
            Q3=makeQuery(id+"F23.imprint","IMPRINT",FACE,{"disambiguationData":[TD([[makeQuery(id+"F23.imprint","IMPRINT",EDGE,{"derivedFrom":sQuery(id+"F23.wireOp",EDGE,"E174.0.2.0")}),-1.0]])]});
            var Q4;
            Q4=makeQuery(id+"F23.imprint","IMPRINT",FACE,{"disambiguationData":[TD([[makeQuery(id+"F23.imprint","IMPRINT",EDGE,{"derivedFrom":sQuery(id+"F23.wireOp",EDGE,"E174.0.1.0")}),-1.0]])]});
            var Q5;
            Q5=makeQuery(id+"F23.imprint","IMPRINT",FACE,{"disambiguationData":[TD([[makeQuery(id+"F23.imprint","IMPRINT",EDGE,{"derivedFrom":sQuery(id+"F23.wireOp",EDGE,"E167.bottom")}),1.0]])]});
            var Q6;
            Q6=makeQuery(id+"F23.imprint","IMPRINT",FACE,{"disambiguationData":[TD([[makeQuery(id+"F23.imprint","IMPRINT",EDGE,{"derivedFrom":sQuery(id+"F23.wireOp",EDGE,"E173.bottom")}),-1.0]])]});
            var Q7;
            Q7=makeQuery(id+"F23.imprint","IMPRINT",FACE,{"disambiguationData":[TD([[makeQuery(id+"F23.imprint","IMPRINT",EDGE,{"derivedFrom":sQuery(id+"F23.wireOp",EDGE,"E169.bottom")}),1.0]])]});
            var Q8;
            Q8=makeQuery(id+"F23.imprint","IMPRINT",FACE,{"disambiguationData":[TD([[makeQuery(id+"F23.imprint","IMPRINT",EDGE,{"derivedFrom":sQuery(id+"F23.wireOp",EDGE,"E168.bottom")}),1.0]])]});
            var Q9;
            Q9=makeQuery(id+"F23.imprint","IMPRINT",FACE,{"disambiguationData":[TD([[makeQuery(id+"F23.imprint","IMPRINT",EDGE,{"derivedFrom":sQuery(id+"F23.wireOp",EDGE,"E171.bottom")}),-1.0]])]});
            var Q10;
            Q10=makeQuery(id+"F23.imprint","IMPRINT",FACE,{"disambiguationData":[TD([[makeQuery(id+"F23.imprint","IMPRINT",EDGE,{"derivedFrom":sQuery(id+"F23.wireOp",EDGE,"E172.bottom")}),-1.0]])]});
            var Q11;
            Q11=makeQuery(id+"F23.imprint","IMPRINT",FACE,{"disambiguationData":[TD([[makeQuery(id+"F23.imprint","IMPRINT",EDGE,{"derivedFrom":sQuery(id+"F23.wireOp",EDGE,"E175.bottom")}),-1.0]])]});
            var Q12;
            Q12=makeQuery(id+"F23.imprint","IMPRINT",FACE,{"disambiguationData":[TD([[makeQuery(id+"F23.imprint","IMPRINT",EDGE,{"derivedFrom":sQuery(id+"F23.wireOp",EDGE,"E179.bottom")}),-1.0]])]});
            var Q13;
            Q13=makeQuery(id+"F23.imprint","IMPRINT",FACE,{"disambiguationData":[TD([[makeQuery(id+"F23.imprint","IMPRINT",EDGE,{"derivedFrom":sQuery(id+"F23.wireOp",EDGE,"E178.bottom")}),-1.0]])]});
            var Q14;
            Q14=makeQuery(id+"F23.imprint","IMPRINT",FACE,{"disambiguationData":[TD([[makeQuery(id+"F23.imprint","IMPRINT",EDGE,{"derivedFrom":sQuery(id+"F23.wireOp",EDGE,"E182.bottom")}),1.0]])]});
            var Q15;
            Q15=makeQuery(id+"F23.imprint","IMPRINT",FACE,{"disambiguationData":[TD([[makeQuery(id+"F23.imprint","IMPRINT",EDGE,{"derivedFrom":sQuery(id+"F23.wireOp",EDGE,"E181.bottom")}),-1.0]])]});
            var Q16;
            Q16=makeQuery(id+"F23.imprint","IMPRINT",FACE,{"disambiguationData":[TD([[makeQuery(id+"F23.imprint","IMPRINT",EDGE,{"derivedFrom":sQuery(id+"F23.wireOp",EDGE,"E183.bottom")}),1.0]])]});
            var Q17;
            Q17=makeQuery(id+"F23.imprint","IMPRINT",FACE,{"disambiguationData":[TD([[makeQuery(id+"F23.imprint","IMPRINT",EDGE,{"derivedFrom":sQuery(id+"F23.wireOp",EDGE,"E184.bottom")}),-1.0]])]});
            var Q18;
            Q18=makeQuery(id+"F23.imprint","IMPRINT",FACE,{"disambiguationData":[TD([[makeQuery(id+"F23.imprint","IMPRINT",EDGE,{"derivedFrom":sQuery(id+"F23.wireOp",EDGE,"E189.bottom")}),-1.0]])]});
            var Q19;
            Q19=makeQuery(id+"F23.imprint","IMPRINT",FACE,{"disambiguationData":[TD([[makeQuery(id+"F23.imprint","IMPRINT",EDGE,{"derivedFrom":sQuery(id+"F23.wireOp",EDGE,"E187.bottom")}),-1.0]])]});
            var Q20;
            Q20=makeQuery(id+"F23.imprint","IMPRINT",FACE,{"disambiguationData":[TD([[makeQuery(id+"F23.imprint","IMPRINT",EDGE,{"derivedFrom":sQuery(id+"F23.wireOp",EDGE,"E190.bottom")}),1.0]])]});
            var Q21;
            Q21=makeQuery(id+"F23.imprint","IMPRINT",FACE,{"disambiguationData":[TD([[makeQuery(id+"F23.imprint","IMPRINT",EDGE,{"derivedFrom":sQuery(id+"F23.wireOp",EDGE,"E191.bottom")}),-1.0]])]});
            var Q22;
            Q22=makeQuery(id+"F23.imprint","IMPRINT",FACE,{"disambiguationData":[TD([[makeQuery(id+"F23.imprint","IMPRINT",EDGE,{"derivedFrom":sQuery(id+"F23.wireOp",EDGE,"E188.bottom")}),-1.0]])]});
            var Q23;
            Q23=makeQuery(id+"F23.imprint","IMPRINT",FACE,{"disambiguationData":[TD([[makeQuery(id+"F23.imprint","IMPRINT",EDGE,{"derivedFrom":sQuery(id+"F23.wireOp",EDGE,"E186.bottom")}),-1.0]])]});
            var Q24;
            Q24=makeQuery(id+"F23.imprint","IMPRINT",FACE,{"disambiguationData":[TD([[makeQuery(id+"F23.imprint","IMPRINT",EDGE,{"derivedFrom":sQuery(id+"F23.wireOp",EDGE,"E185.bottom")}),-1.0]])]});
            var Q25;
            Q25=makeQuery(id+"F23.imprint","IMPRINT",FACE,{"disambiguationData":[TD([[makeQuery(id+"F23.imprint","IMPRINT",EDGE,{"derivedFrom":sQuery(id+"F23.wireOp",EDGE,"E180.bottom")}),-1.0]])]});
            var Q26;
            Q26=makeQuery(id+"F23.imprint","IMPRINT",FACE,{"disambiguationData":[TD([[makeQuery(id+"F23.imprint","IMPRINT",EDGE,{"derivedFrom":sQuery(id+"F23.wireOp",EDGE,"E196.bottom")}),1.0]])]});
            var Q27;
            Q27=makeQuery(id+"F23.imprint","IMPRINT",FACE,{"disambiguationData":[TD([[makeQuery(id+"F23.imprint","IMPRINT",EDGE,{"derivedFrom":sQuery(id+"F23.wireOp",EDGE,"E195.bottom")}),1.0]])]});
            var Q28;
            Q28=makeQuery(id+"F23.imprint","IMPRINT",FACE,{"disambiguationData":[TD([[makeQuery(id+"F23.imprint","IMPRINT",EDGE,{"derivedFrom":sQuery(id+"F23.wireOp",EDGE,"E197.bottom")}),-1.0]])]});
            var Q29;
            Q29=makeQuery(id+"F23.imprint","IMPRINT",FACE,{"disambiguationData":[TD([[makeQuery(id+"F23.imprint","IMPRINT",EDGE,{"derivedFrom":sQuery(id+"F23.wireOp",EDGE,"E194.bottom")}),-1.0]])]});
            var Q30;
            Q30=makeQuery(id+"F23.imprint","IMPRINT",FACE,{"disambiguationData":[TD([[makeQuery(id+"F23.imprint","IMPRINT",EDGE,{"derivedFrom":sQuery(id+"F23.wireOp",EDGE,"E206.bottom")}),1.0]])]});
            var Q31;
            Q31=makeQuery(id+"F23.imprint","IMPRINT",FACE,{"disambiguationData":[TD([[makeQuery(id+"F23.imprint","IMPRINT",EDGE,{"derivedFrom":sQuery(id+"F23.wireOp",EDGE,"E198.bottom")}),-1.0]])]});
            var Q32;
            Q32=makeQuery(id+"F23.imprint","IMPRINT",FACE,{"disambiguationData":[TD([[makeQuery(id+"F23.imprint","IMPRINT",EDGE,{"derivedFrom":sQuery(id+"F23.wireOp",EDGE,"E199.bottom")}),1.0]])]});
            var Q33;
            Q33=makeQuery(id+"F23.imprint","IMPRINT",FACE,{"disambiguationData":[TD([[makeQuery(id+"F23.imprint","IMPRINT",EDGE,{"derivedFrom":sQuery(id+"F23.wireOp",EDGE,"E200.bottom")}),-1.0]])]});
            var Q34;
            Q34=makeQuery(id+"F23.imprint","IMPRINT",FACE,{"disambiguationData":[TD([[makeQuery(id+"F23.imprint","IMPRINT",EDGE,{"derivedFrom":sQuery(id+"F23.wireOp",EDGE,"E201.bottom")}),1.0]])]});
            var Q35;
            Q35=makeQuery(id+"F23.imprint","IMPRINT",FACE,{"disambiguationData":[TD([[makeQuery(id+"F23.imprint","IMPRINT",EDGE,{"derivedFrom":sQuery(id+"F23.wireOp",EDGE,"E203.bottom")}),1.0]])]});
            var Q36;
            Q36=makeQuery(id+"F23.imprint","IMPRINT",FACE,{"disambiguationData":[TD([[makeQuery(id+"F23.imprint","IMPRINT",EDGE,{"derivedFrom":sQuery(id+"F23.wireOp",EDGE,"E204.bottom")}),1.0]])]});
            var Q37;
            Q37=makeQuery(id+"F23.imprint","IMPRINT",FACE,{"disambiguationData":[TD([[makeQuery(id+"F23.imprint","IMPRINT",EDGE,{"derivedFrom":sQuery(id+"F23.wireOp",EDGE,"E205.bottom")}),1.0]])]});
            var Q38;
            Q38=makeQuery(id+"F23.imprint","IMPRINT",FACE,{"disambiguationData":[TD([[makeQuery(id+"F23.imprint","IMPRINT",EDGE,{"derivedFrom":sQuery(id+"F23.wireOp",EDGE,"E193.bottom")}),-1.0]])]});
            var Q39;
            Q39=makeQuery(id+"F23.imprint","IMPRINT",FACE,{"disambiguationData":[TD([[makeQuery(id+"F23.imprint","IMPRINT",EDGE,{"derivedFrom":sQuery(id+"F23.wireOp",EDGE,"E192.bottom")}),1.0]])]});
            var Q40;
            Q40=makeQuery(id+"F23.imprint","IMPRINT",FACE,{"disambiguationData":[TD([[makeQuery(id+"F23.imprint","IMPRINT",EDGE,{"derivedFrom":sQuery(id+"F23.wireOp",EDGE,"E202.bottom")}),1.0]])]});
            var Q41;
            Q41=makeQuery(id+"F23.imprint","IMPRINT",FACE,{"disambiguationData":[TD([[makeQuery(id+"F23.imprint","IMPRINT",EDGE,{"derivedFrom":sQuery(id+"F23.wireOp",EDGE,"E215.bottom")}),1.0]])]});
            var Q42;
            Q42=makeQuery(id+"F23.imprint","IMPRINT",FACE,{"disambiguationData":[TD([[makeQuery(id+"F23.imprint","IMPRINT",EDGE,{"derivedFrom":sQuery(id+"F23.wireOp",EDGE,"E214.bottom")}),1.0]])]});
            var Q43;
            Q43=makeQuery(id+"F23.imprint","IMPRINT",FACE,{"disambiguationData":[TD([[makeQuery(id+"F23.imprint","IMPRINT",EDGE,{"derivedFrom":sQuery(id+"F23.wireOp",EDGE,"E216.bottom")}),1.0]])]});
            var Q44;
            Q44=makeQuery(id+"F23.imprint","IMPRINT",FACE,{"disambiguationData":[TD([[makeQuery(id+"F23.imprint","IMPRINT",EDGE,{"derivedFrom":sQuery(id+"F23.wireOp",EDGE,"E208.bottom")}),1.0]])]});
            var Q45;
            Q45=makeQuery(id+"F23.imprint","IMPRINT",FACE,{"disambiguationData":[TD([[makeQuery(id+"F23.imprint","IMPRINT",EDGE,{"derivedFrom":sQuery(id+"F23.wireOp",EDGE,"E209.bottom")}),-1.0]])]});
            var Q46;
            Q46=makeQuery(id+"F23.imprint","IMPRINT",FACE,{"disambiguationData":[TD([[makeQuery(id+"F23.imprint","IMPRINT",EDGE,{"derivedFrom":sQuery(id+"F23.wireOp",EDGE,"E207.bottom")}),1.0]])]});
            var Q47;
            Q47=makeQuery(id+"F23.imprint","IMPRINT",FACE,{"disambiguationData":[TD([[makeQuery(id+"F23.imprint","IMPRINT",EDGE,{"derivedFrom":sQuery(id+"F23.wireOp",EDGE,"E211.bottom")}),1.0]])]});
            var Q48;
            Q48=makeQuery(id+"F23.imprint","IMPRINT",FACE,{"disambiguationData":[TD([[makeQuery(id+"F23.imprint","IMPRINT",EDGE,{"derivedFrom":sQuery(id+"F23.wireOp",EDGE,"E210.bottom")}),1.0]])]});
            var Q49;
            Q49=makeQuery(id+"F23.imprint","IMPRINT",FACE,{"disambiguationData":[TD([[makeQuery(id+"F23.imprint","IMPRINT",EDGE,{"derivedFrom":sQuery(id+"F23.wireOp",EDGE,"E212.bottom")}),1.0]])]});
            var Q50;
            Q50=makeQuery(id+"F23.imprint","IMPRINT",FACE,{"disambiguationData":[TD([[makeQuery(id+"F23.imprint","IMPRINT",EDGE,{"derivedFrom":sQuery(id+"F23.wireOp",EDGE,"E213.bottom")}),1.0]])]});
            var Q51;
            Q51=makeQuery(id+"F23.imprint","IMPRINT",FACE,{"disambiguationData":[TD([[makeQuery(id+"F23.imprint","IMPRINT",EDGE,{"derivedFrom":sQuery(id+"F23.wireOp",EDGE,"E217.bottom")}),-1.0]])]});
            var Q52;
            Q52=makeQuery(id+"F23.imprint","IMPRINT",FACE,{"disambiguationData":[TD([[makeQuery(id+"F23.imprint","IMPRINT",EDGE,{"derivedFrom":sQuery(id+"F23.wireOp",EDGE,"E218.bottom")}),-1.0]])]});
            var Q53;
            Q53=makeQuery(id+"F23.imprint","IMPRINT",FACE,{"disambiguationData":[TD([[makeQuery(id+"F23.imprint","IMPRINT",EDGE,{"derivedFrom":sQuery(id+"F23.wireOp",EDGE,"E219.bottom")}),-1.0]])]});
            var Q54;
            Q54=makeQuery(id+"F23.imprint","IMPRINT",FACE,{"disambiguationData":[TD([[makeQuery(id+"F23.imprint","IMPRINT",EDGE,{"derivedFrom":sQuery(id+"F23.wireOp",EDGE,"E220.bottom")}),-1.0]])]});
            var Q55;
            Q55=makeQuery(id+"F23.imprint","IMPRINT",FACE,{"disambiguationData":[TD([[makeQuery(id+"F23.imprint","IMPRINT",EDGE,{"derivedFrom":sQuery(id+"F23.wireOp",EDGE,"E221.bottom")}),-1.0]])]});
            var Q56;
            Q56=makeQuery(id+"F23.imprint","IMPRINT",FACE,{"disambiguationData":[TD([[makeQuery(id+"F23.imprint","IMPRINT",EDGE,{"derivedFrom":sQuery(id+"F23.wireOp",EDGE,"E223.bottom")}),-1.0]])]});
            var Q57;
            Q57=makeQuery(id+"F23.imprint","IMPRINT",FACE,{"disambiguationData":[TD([[makeQuery(id+"F23.imprint","IMPRINT",EDGE,{"derivedFrom":sQuery(id+"F23.wireOp",EDGE,"E222.bottom")}),-1.0]])]});
            extrude(context, id + "F24", {"entities" : qUnion([Q0, Q1, Q2, Q3, Q4, Q5, Q6, Q7, Q8, Q9, Q10, Q11, Q12, Q13, Q14, Q15, Q16, Q17, Q18, Q19, Q20, Q21, Q22, Q23, Q24, Q25, Q26, Q27, Q28, Q29, Q30, Q31, Q32, Q33, Q34, Q35, Q36, Q37, Q38, Q39, Q40, Q41, Q42, Q43, Q44, Q45, Q46, Q47, Q48, Q49, Q50, Q51, Q52, Q53, Q54, Q55, Q56, Q57]), "operationType" : NewBodyOperationType.ADD, "depth" : 0.8 * mm});
        }
        {
            var Q0;
            Q0=makeQuery(id+"F24.opExtrude","CAP_FACE",FACE,{"disambiguationData":[OSD([sQuery(id+"F23.wireOp",EDGE,"E175.bottom"),sQuery(id+"F23.wireOp",EDGE,"E175.top"),sQuery(id+"F23.wireOp",EDGE,"E175.left"),sQuery(id+"F23.wireOp",EDGE,"E175.right")])],"isStart":true});
            extrude(context, id + "F25", {"entities" : qUnion([Q0]), "operationType" : NewBodyOperationType.ADD, "depth" : 0.8 * mm, "hasSecondDirection" : true, "secondDirectionOppositeDirection" : true, "secondDirectionDepth" : 1.75 * mm});
        }
        {
            var Q0;
            {var subQ0=sQuery(id+"F23.wireOp",EDGE,"E175.bottom");Q0=makeQuery(id+"F25.boolean.opBoolean","MERGE",FACE,{"derivedFrom":[makeQuery(id+"F2.opExtrude","SWEPT_FACE",FACE,{"disambiguationData":[OSD([sQuery(id+"F0.wireOp",EDGE,"E51.top")])]}),makeQuery(id+"F24.opExtrude","SWEPT_FACE",FACE,{"disambiguationData":[OSD([subQ0])]}),makeQuery(id+"F25.opExtrude","SWEPT_FACE",FACE,{"disambiguationData":[OSD([subQ0])]})]});}
            var sketch = newSketch(context, id + "F26", { "sketchPlane" : qUnion([Q0])});
            skLineSegment(sketch, "E224", {"start": v(-42.84, 3.08) * mm, "end": v(-42.84, 2.06) * mm});
            skLineSegment(sketch, "E225", {"start": v(-42.84, 2.06) * mm, "end": v(-41.78, 1.17) * mm});
            skLineSegment(sketch, "E226", {"start": v(-41.78, 1.17) * mm, "end": v(-36.96, 1.17) * mm});
            skLineSegment(sketch, "E227", {"start": v(-36.96, 1.17) * mm, "end": v(-35.9, 2.06) * mm});
            skLineSegment(sketch, "E228", {"start": v(-35.9, 2.06) * mm, "end": v(-35.9, 3.08) * mm});
            skLineSegment(sketch, "E229", {"start": v(-35.9, 3.08) * mm, "end": v(-42.84, 3.08) * mm});
            skPoint(sketch, "E230", {"position": v(-39.37, 3.33) * mm});
            skPoint(sketch, "E231", {"position": v(-39.37, 3.08) * mm});
            skPoint(sketch, "E232", {"position": v(-39.37, 1.17) * mm});
            skLineSegment(sketch, "E233", {"start": v(-43.18, 0.8) * mm, "end": v(-41.78, 0.8) * mm});
            skLineSegment(sketch, "E234", {"start": v(-41.78, 0.8) * mm, "end": v(-43.18, 1.97) * mm});
            skLineSegment(sketch, "E235", {"start": v(-35.56, 0.8) * mm, "end": v(-36.96, 0.8) * mm});
            skLineSegment(sketch, "E236", {"start": v(-36.96, 0.8) * mm, "end": v(-35.56, 1.97) * mm});
            skSolve(sketch);
        }
        {
            var Q0;
            {var subQ0=sQuery(id+"F26.wireOp",EDGE,"E233");Q0=makeQuery(id+"F26.imprint","IMPRINT",FACE,{"disambiguationData":[TD([[makeQuery(id+"F26.imprint","IMPRINT",EDGE,{"derivedFrom":subQ0}),1.0]])]});}
            var Q1;
            {var subQ0=sQuery(id+"F26.wireOp",EDGE,"E235");Q1=makeQuery(id+"F26.imprint","IMPRINT",FACE,{"disambiguationData":[TD([[makeQuery(id+"F26.imprint","IMPRINT",EDGE,{"derivedFrom":subQ0}),-1.0]])]});}
            var Q2;
            Q2=makeQuery(id+"F26.imprint","IMPRINT",FACE,{"disambiguationData":[TD([[makeQuery(id+"F26.imprint","IMPRINT",EDGE,{"derivedFrom":sQuery(id+"F26.wireOp",EDGE,"E224")}),1.0]])]});
            extrude(context, id + "F27", {"entities" : qUnion([Q0, Q1, Q2]), "operationType" : NewBodyOperationType.REMOVE, "oppositeDirection" : true, "depth" : 5.08 * mm});
        }
        {
            var Q0;
            Q0=makeQuery(id+"F1.opExtrude","CAP_FACE",FACE,{"disambiguationData":[OSD([sQuery(id+"F0.wireOp",EDGE,"E9.bottom"),sQuery(id+"F0.wireOp",EDGE,"E9.top"),sQuery(id+"F0.wireOp",EDGE,"E9.left"),sQuery(id+"F0.wireOp",EDGE,"E9.right"),sQuery(id+"F0.wireOp",EDGE,"E10.filletArc"),sQuery(id+"F0.wireOp",EDGE,"E11.filletArc"),sQuery(id+"F0.wireOp",EDGE,"E12.filletArc"),sQuery(id+"F0.wireOp",EDGE,"E13.filletArc"),sQuery(id+"F0.wireOp",EDGE,"E14"),sQuery(id+"F0.wireOp",EDGE,"E15"),sQuery(id+"F0.wireOp",EDGE,"E16"),sQuery(id+"F0.wireOp",EDGE,"E17.1.0.0"),sQuery(id+"F0.wireOp",EDGE,"E17.2.0.0"),sQuery(id+"F0.wireOp",EDGE,"E17.3.0.0"),sQuery(id+"F0.wireOp",EDGE,"E17.4.0.0"),sQuery(id+"F0.wireOp",EDGE,"E17.5.0.0"),sQuery(id+"F0.wireOp",EDGE,"E17.6.0.0"),sQuery(id+"F0.wireOp",EDGE,"E17.7.0.0"),sQuery(id+"F0.wireOp",EDGE,"E28"),sQuery(id+"F0.wireOp",EDGE,"E29"),sQuery(id+"F0.wireOp",EDGE,"E30")])],"isStart":false});
            var sketch = newSketch(context, id + "F28", { "sketchPlane" : qUnion([Q0])});
            skText(sketch, "E237", { "text": "LIS3DH", "fontName": "OpenSans-Regular.ttf"});
            skPoint(sketch, "E238", {"position": v(-16.51, 20.32) * mm});
            skText(sketch, "E239", { "text": "TCS34725", "fontName": "OpenSans-Regular.ttf"});
            skLineSegment(sketch, "E240.0", {"start": v(-8.89, -6.35) * mm, "end": v(-24.13, -6.35) * mm, "construction": true});
            skPoint(sketch, "E241", {"position": v(-16.51, -6.35) * mm});
            skText(sketch, "E242", { "text": "RGB Sensor", "fontName": "OpenSans-Regular.ttf"});
            skText(sketch, "E243", { "text": "MAX98306", "fontName": "OpenSans-Regular.ttf"});
            skLineSegment(sketch, "E244.0", {"start": v(2.54, -6.35) * mm, "end": v(21.59, -6.35) * mm});
            skPoint(sketch, "E245", {"position": v(12.06, -6.35) * mm});
            skText(sketch, "E246", { "text": "Stereo Amplifier", "fontName": "OpenSans-Regular.ttf"});
            skText(sketch, "E247", { "text": "Bluefruit LE SPI", "fontName": "OpenSans-Regular.ttf"});
            skLineSegment(sketch, "E248.0", {"start": v(0, 0) * mm, "end": v(0, 22.86) * mm});
            skText(sketch, "E249", { "text": "TSL2561", "fontName": "OpenSans-Regular.ttf"});
            skText(sketch, "E250", { "text": "Lux Sensor", "fontName": "OpenSans-Regular.ttf"});
            skText(sketch, "E251", { "text": "MCP9808", "fontName": "OpenSans-Regular.ttf"});
            const initialGuessF28  = {"E237": [-0.0216, 0.01734, 1, 0, 0.00218], "E239": [-0.0216, -0.00873, 1, 0, 0.0016], "E242": [-0.02223, -0.01048, 1, 0, 0.0015], "E243": [0.00492, -0.0092, 1, 0, 0.00206], "E246": [0.00413, -0.01097, 1, 0, 0.0015], "E247": [0.00194, 0.00476, 0, 1, 0.00156], "E249": [0.03353, -0.009, 1, 0, 0.00185], "E250": [0.03353, -0.01075, 1, 0, 0.0015], "E251": [0.03327, 0.02644, 1, 0, 0.00198]};
            skSetInitialGuess(sketch, initialGuessF28);
            skSolve(sketch);
        }
        {
            var Q0;
            Q0=qSketchRegion(id+"F28",true);
            extrude(context, id + "F29", {"entities" : qUnion([Q0]), "operationType" : NewBodyOperationType.REMOVE, "oppositeDirection" : true, "depth" : 0.25 * mm});
        }
        {
            var Q0;
            Q0=makeQuery(id+"F27.boolean.opBoolean","MERGE",FACE,{"derivedFrom":[makeQuery(id+"F2.opExtrude","CAP_FACE",FACE,{"disambiguationData":[OSD([sQuery(id+"F0.wireOp",EDGE,"E51.bottom"),sQuery(id+"F0.wireOp",EDGE,"E51.top"),sQuery(id+"F0.wireOp",EDGE,"E51.left"),sQuery(id+"F0.wireOp",EDGE,"E51.right"),sQuery(id+"F0.wireOp",EDGE,"E52.filletArc"),sQuery(id+"F0.wireOp",EDGE,"E53.filletArc"),sQuery(id+"F0.wireOp",EDGE,"E54.filletArc"),sQuery(id+"F0.wireOp",EDGE,"E55.filletArc"),sQuery(id+"F0.wireOp",EDGE,"E56"),sQuery(id+"F0.wireOp",EDGE,"E57"),sQuery(id+"F0.wireOp",EDGE,"E58"),sQuery(id+"F0.wireOp",EDGE,"E59"),sQuery(id+"F0.wireOp",EDGE,"E60"),sQuery(id+"F0.wireOp",EDGE,"E61"),sQuery(id+"F0.wireOp",EDGE,"E62")])],"isStart":false}),makeQuery(id+"F27.opExtrude","SWEPT_FACE",FACE,{"disambiguationData":[OSD([sQuery(id+"F26.wireOp",EDGE,"E233")])]}),makeQuery(id+"F27.opExtrude","SWEPT_FACE",FACE,{"disambiguationData":[OSD([sQuery(id+"F26.wireOp",EDGE,"E235")])]})]});
            var sketch = newSketch(context, id + "F30", { "sketchPlane" : qUnion([Q0])});
            skText(sketch, "E252", { "text": "USB", "fontName": "OpenSans-Regular.ttf"});
            skText(sketch, "E253", { "text": "Micro", "fontName": "OpenSans-Regular.ttf"});
            const initialGuessF30  = {"E252": [0.03142, 0.00159, 0, 1, 0.00142], "E253": [0.03297, 0.00111, 0, 1, 0.0013]};
            skSetInitialGuess(sketch, initialGuessF30);
            skSolve(sketch);
        }
        {
            var Q0;
            Q0=qSketchRegion(id+"F30",true);
            extrude(context, id + "F31", {"entities" : qUnion([Q0]), "operationType" : NewBodyOperationType.REMOVE, "oppositeDirection" : true, "depth" : 0.25 * mm});
        }
    });